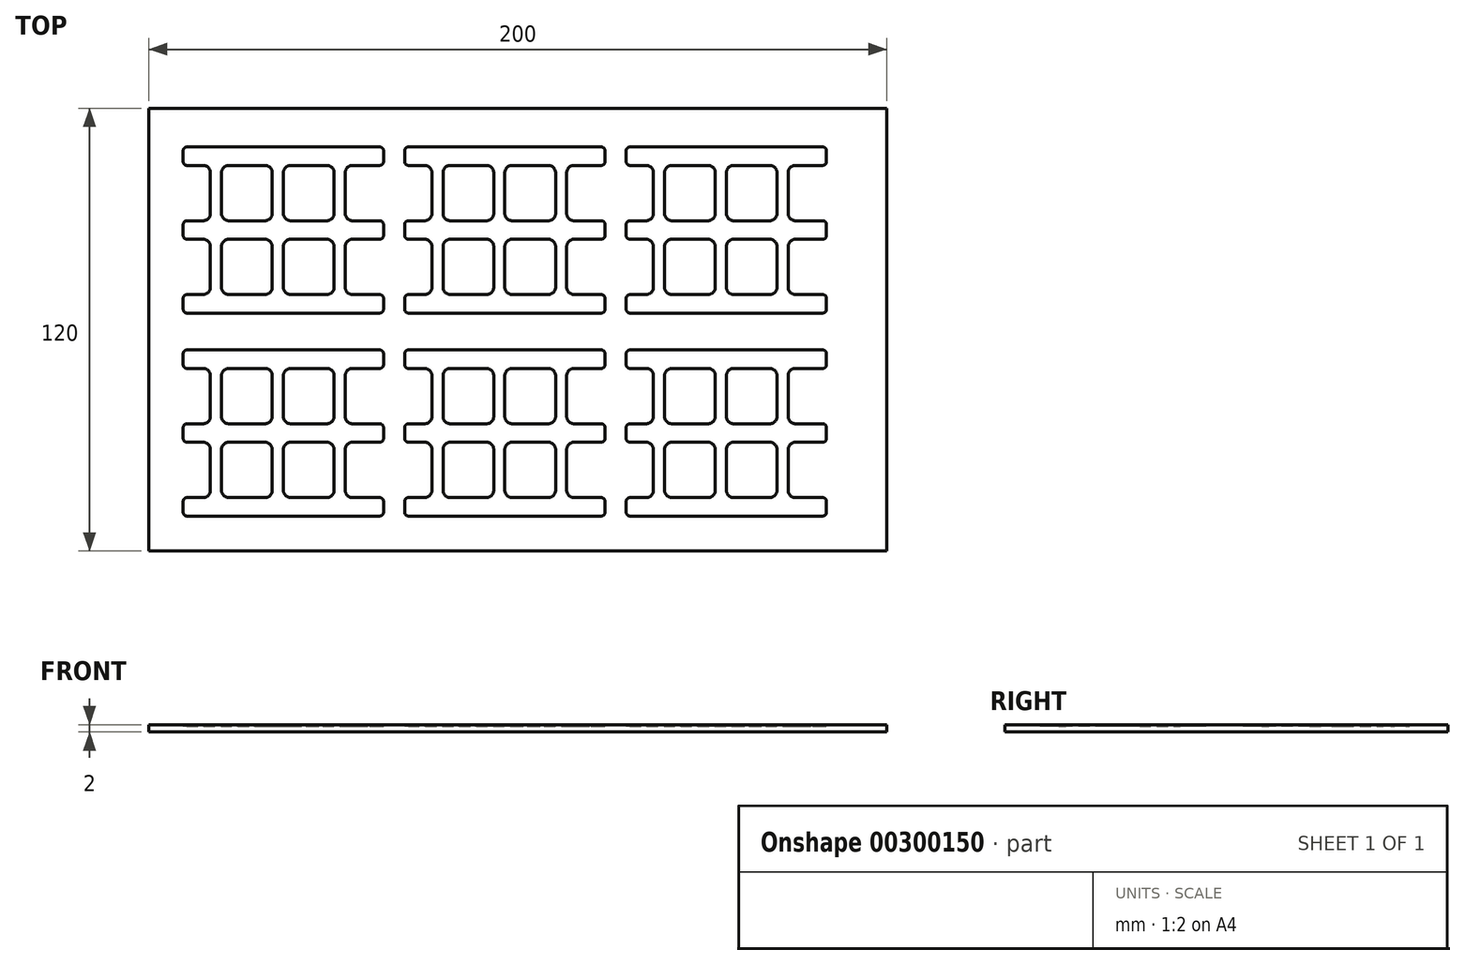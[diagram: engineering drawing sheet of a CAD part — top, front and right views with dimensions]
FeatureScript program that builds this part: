
annotation { "Feature Type Name" : "Feature", "Feature Type Description" : "" }
export const myFeature = defineFeature(function(context is Context, id is Id, definition is map)
    precondition{}
    {
        {
            var Q0;
            Q0=qCreatedBy(makeId("Top.planeOp"),FACE);
            var sketch = newSketch(context, id + "F0", { "sketchPlane" : qUnion([Q0])});
            skLineSegment(sketch, "E0.bottom", {"start": v(-3.5, 2.5) * mm, "end": v(-13.25, 2.5) * mm});
            skLineSegment(sketch, "E0.top", {"start": v(-3.5, 17.5) * mm, "end": v(-13.25, 17.5) * mm});
            skLineSegment(sketch, "E0.left", {"start": v(-1.5, 4.5) * mm, "end": v(-1.5, 15.5) * mm});
            skLineSegment(sketch, "E0.right", {"start": v(-15.25, 4.5) * mm, "end": v(-15.25, 15.5) * mm});
            skPoint(sketch, "E1.visualSharp", {"position": v(-15.25, 17.5) * mm});
            skArc(sketch, "E1.filletArc", {"start": v(-13.25, 17.5) * mm, "mid": v(-14.66, 16.91) * mm, "end": v(-15.25, 15.5) * mm});
            skPoint(sketch, "E2.visualSharp", {"position": v(-1.5, 17.5) * mm});
            skArc(sketch, "E2.filletArc", {"start": v(-1.5, 15.5) * mm, "mid": v(-2.09, 16.91) * mm, "end": v(-3.5, 17.5) * mm});
            skPoint(sketch, "E3.visualSharp", {"position": v(-1.5, 2.5) * mm});
            skArc(sketch, "E3.filletArc", {"start": v(-3.5, 2.5) * mm, "mid": v(-2.09, 3.09) * mm, "end": v(-1.5, 4.5) * mm});
            skPoint(sketch, "E4.visualSharp", {"position": v(-15.25, 2.5) * mm});
            skArc(sketch, "E4.filletArc", {"start": v(-15.25, 4.5) * mm, "mid": v(-14.66, 3.09) * mm, "end": v(-13.25, 2.5) * mm});
            skArc(sketch, "E5.MirrorCS", {"start": v(15.25, 4.5) * mm, "mid": v(14.66, 3.09) * mm, "end": v(13.25, 2.5) * mm});
            skArc(sketch, "E6.MirrorCS", {"start": v(13.25, 17.5) * mm, "mid": v(14.66, 16.91) * mm, "end": v(15.25, 15.5) * mm});
            skArc(sketch, "E7.MirrorCS", {"start": v(3.5, 2.5) * mm, "mid": v(2.09, 3.09) * mm, "end": v(1.5, 4.5) * mm});
            skArc(sketch, "E8.MirrorCS", {"start": v(1.5, 15.5) * mm, "mid": v(2.09, 16.91) * mm, "end": v(3.5, 17.5) * mm});
            skLineSegment(sketch, "E9.MirrorCS", {"start": v(3.5, 17.5) * mm, "end": v(13.25, 17.5) * mm});
            skLineSegment(sketch, "E10.MirrorCS", {"start": v(1.5, 4.5) * mm, "end": v(1.5, 15.5) * mm});
            skPoint(sketch, "E11.MirrorP", {"position": v(1.5, 17.5) * mm});
            skPoint(sketch, "E12.MirrorP", {"position": v(15.25, 2.5) * mm});
            skPoint(sketch, "E13.MirrorP", {"position": v(15.25, 17.5) * mm});
            skPoint(sketch, "E14.MirrorP", {"position": v(1.5, 2.5) * mm});
            skLineSegment(sketch, "E15.MirrorCS", {"start": v(3.5, 2.5) * mm, "end": v(13.25, 2.5) * mm});
            skLineSegment(sketch, "E16.MirrorCS", {"start": v(15.25, 4.5) * mm, "end": v(15.25, 15.5) * mm});
            skArc(sketch, "E17.MirrorCS", {"start": v(-1.5, -15.5) * mm, "mid": v(-2.09, -16.91) * mm, "end": v(-3.5, -17.5) * mm});
            skArc(sketch, "E18.MirrorCS", {"start": v(-3.5, -2.5) * mm, "mid": v(-2.09, -3.09) * mm, "end": v(-1.5, -4.5) * mm});
            skArc(sketch, "E19.MirrorCS", {"start": v(-13.25, -17.5) * mm, "mid": v(-14.66, -16.91) * mm, "end": v(-15.25, -15.5) * mm});
            skArc(sketch, "E20.MirrorCS", {"start": v(15.25, -4.5) * mm, "mid": v(14.66, -3.09) * mm, "end": v(13.25, -2.5) * mm});
            skArc(sketch, "E21.MirrorCS", {"start": v(-15.25, -4.5) * mm, "mid": v(-14.66, -3.09) * mm, "end": v(-13.25, -2.5) * mm});
            skArc(sketch, "E22.MirrorCS", {"start": v(13.25, -17.5) * mm, "mid": v(14.66, -16.91) * mm, "end": v(15.25, -15.5) * mm});
            skArc(sketch, "E23.MirrorCS", {"start": v(3.5, -2.5) * mm, "mid": v(2.09, -3.09) * mm, "end": v(1.5, -4.5) * mm});
            skArc(sketch, "E24.MirrorCS", {"start": v(1.5, -15.5) * mm, "mid": v(2.09, -16.91) * mm, "end": v(3.5, -17.5) * mm});
            skPoint(sketch, "E25.MirrorP", {"position": v(-15.25, -2.5) * mm});
            skLineSegment(sketch, "E26.MirrorCS", {"start": v(-1.5, -4.5) * mm, "end": v(-1.5, -15.5) * mm});
            skLineSegment(sketch, "E27.MirrorCS", {"start": v(15.25, -4.5) * mm, "end": v(15.25, -15.5) * mm});
            skPoint(sketch, "E28.MirrorP", {"position": v(-15.25, -17.5) * mm});
            skLineSegment(sketch, "E29.MirrorCS", {"start": v(3.5, -17.5) * mm, "end": v(13.25, -17.5) * mm});
            skLineSegment(sketch, "E30.MirrorCS", {"start": v(-15.25, -4.5) * mm, "end": v(-15.25, -15.5) * mm});
            skLineSegment(sketch, "E31.MirrorCS", {"start": v(-3.5, -17.5) * mm, "end": v(-13.25, -17.5) * mm});
            skPoint(sketch, "E32.MirrorP", {"position": v(-1.5, -17.5) * mm});
            skLineSegment(sketch, "E33.MirrorCS", {"start": v(1.5, -4.5) * mm, "end": v(1.5, -15.5) * mm});
            skLineSegment(sketch, "E34.MirrorCS", {"start": v(-3.5, -2.5) * mm, "end": v(-13.25, -2.5) * mm});
            skPoint(sketch, "E35.MirrorP", {"position": v(1.5, -17.5) * mm});
            skPoint(sketch, "E36.MirrorP", {"position": v(-1.5, -2.5) * mm});
            skPoint(sketch, "E37.MirrorP", {"position": v(15.25, -2.5) * mm});
            skPoint(sketch, "E38.MirrorP", {"position": v(15.25, -17.5) * mm});
            skPoint(sketch, "E39.MirrorP", {"position": v(1.5, -2.5) * mm});
            skLineSegment(sketch, "E40.MirrorCS", {"start": v(3.5, -2.5) * mm, "end": v(13.25, -2.5) * mm});
            skLineSegment(sketch, "E41", {"start": v(16.75, 36.36) * mm, "end": v(16.75, -33.16) * mm, "construction": true});
            skArc(sketch, "E42.MirrorCS", {"start": v(18.25, 4.5) * mm, "mid": v(18.84, 3.09) * mm, "end": v(20.25, 2.5) * mm});
            skArc(sketch, "E43.MirrorCS", {"start": v(20.25, -17.5) * mm, "mid": v(18.84, -16.91) * mm, "end": v(18.25, -15.5) * mm});
            skArc(sketch, "E44.MirrorCS", {"start": v(20.25, 17.5) * mm, "mid": v(18.84, 16.91) * mm, "end": v(18.25, 15.5) * mm});
            skArc(sketch, "E45.MirrorCS", {"start": v(18.25, -4.5) * mm, "mid": v(18.84, -3.09) * mm, "end": v(20.25, -2.5) * mm});
            skLineSegment(sketch, "E46.MirrorCS", {"start": v(25.63, -2.5) * mm, "end": v(20.25, -2.5) * mm});
            skLineSegment(sketch, "E47.MirrorCS", {"start": v(18.25, -4.5) * mm, "end": v(18.25, -15.5) * mm});
            skPoint(sketch, "E48.MirrorP", {"position": v(18.25, 2.5) * mm});
            skPoint(sketch, "E49.MirrorP", {"position": v(18.25, -2.5) * mm});
            skLineSegment(sketch, "E50.MirrorCS", {"start": v(25.63, 17.5) * mm, "end": v(20.25, 17.5) * mm});
            skPoint(sketch, "E51.MirrorP", {"position": v(18.25, -17.5) * mm});
            skLineSegment(sketch, "E52.MirrorCS", {"start": v(25.63, -17.5) * mm, "end": v(20.25, -17.5) * mm});
            skLineSegment(sketch, "E53.MirrorCS", {"start": v(18.25, 4.5) * mm, "end": v(18.25, 15.5) * mm});
            skPoint(sketch, "E54.MirrorP", {"position": v(18.25, 17.5) * mm});
            skLineSegment(sketch, "E55.MirrorCS", {"start": v(25.63, 2.5) * mm, "end": v(20.25, 2.5) * mm});
            skLineSegment(sketch, "E56.bottom", {"start": v(25.63, 22.5) * mm, "end": v(-24.62, 22.5) * mm});
            skLineSegment(sketch, "E56.top", {"start": v(25.63, -22.5) * mm, "end": v(-24.62, -22.5) * mm});
            skLineSegment(sketch, "E56.left", {"start": v(25.63, 22.5) * mm, "end": v(25.63, 17.5) * mm});
            skPoint(sketch, "E56.middle", {"position": v(0, 0) * mm});
            skArc(sketch, "E57.MirrorCS", {"start": v(-18.25, 4.5) * mm, "mid": v(-18.84, 3.09) * mm, "end": v(-20.25, 2.5) * mm});
            skArc(sketch, "E58.MirrorCS", {"start": v(-18.25, -4.5) * mm, "mid": v(-18.84, -3.09) * mm, "end": v(-20.25, -2.5) * mm});
            skArc(sketch, "E59.MirrorCS", {"start": v(-20.25, 17.5) * mm, "mid": v(-18.84, 16.91) * mm, "end": v(-18.25, 15.5) * mm});
            skArc(sketch, "E60.MirrorCS", {"start": v(-20.25, -17.5) * mm, "mid": v(-18.84, -16.91) * mm, "end": v(-18.25, -15.5) * mm});
            skPoint(sketch, "E61.MirrorP", {"position": v(-18.25, -2.5) * mm});
            skLineSegment(sketch, "E62.MirrorCS", {"start": v(-18.25, -4.5) * mm, "end": v(-18.25, -15.5) * mm});
            skLineSegment(sketch, "E63.MirrorCS", {"start": v(-24.62, -2.5) * mm, "end": v(-20.25, -2.5) * mm});
            skPoint(sketch, "E64.MirrorP", {"position": v(-18.25, 2.5) * mm});
            skPoint(sketch, "E65.MirrorP", {"position": v(-18.25, 17.5) * mm});
            skLineSegment(sketch, "E66.MirrorCS", {"start": v(-25.63, 21.5) * mm, "end": v(-25.63, 18.5) * mm});
            skPoint(sketch, "E67.MirrorP", {"position": v(-18.25, -17.5) * mm});
            skLineSegment(sketch, "E68.MirrorCS", {"start": v(-24.62, 2.5) * mm, "end": v(-20.25, 2.5) * mm});
            skLineSegment(sketch, "E69.MirrorCS", {"start": v(-24.62, -17.5) * mm, "end": v(-20.25, -17.5) * mm});
            skLineSegment(sketch, "E70.MirrorCS", {"start": v(-24.62, 17.5) * mm, "end": v(-20.25, 17.5) * mm});
            skLineSegment(sketch, "E71.MirrorCS", {"start": v(-18.25, 4.5) * mm, "end": v(-18.25, 15.5) * mm});
            skLineSegment(sketch, "E72.trimOffspring", {"start": v(25.63, 2.5) * mm, "end": v(25.63, -2.5) * mm});
            skLineSegment(sketch, "E73.trimOffspring", {"start": v(25.63, -17.5) * mm, "end": v(25.63, -22.5) * mm});
            skLineSegment(sketch, "E74.trimOffspring", {"start": v(-25.63, 1.5) * mm, "end": v(-25.63, -1.5) * mm});
            skLineSegment(sketch, "E75.trimOffspring", {"start": v(-25.63, -18.5) * mm, "end": v(-25.63, -21.5) * mm});
            skLineSegment(sketch, "E76.bottom", {"start": v(25.63, 22.5) * mm, "end": v(27.62, 22.5) * mm});
            skLineSegment(sketch, "E76.top", {"start": v(25.63, 17.5) * mm, "end": v(27.62, 17.5) * mm});
            skLineSegment(sketch, "E76.right", {"start": v(28.62, 21.5) * mm, "end": v(28.62, 18.5) * mm});
            skLineSegment(sketch, "E77.bottom", {"start": v(25.63, 2.5) * mm, "end": v(27.62, 2.5) * mm});
            skLineSegment(sketch, "E77.top", {"start": v(25.63, -2.5) * mm, "end": v(27.62, -2.5) * mm});
            skLineSegment(sketch, "E77.right", {"start": v(28.62, 1.5) * mm, "end": v(28.62, -1.5) * mm});
            skLineSegment(sketch, "E78.bottom", {"start": v(25.63, -17.5) * mm, "end": v(27.63, -17.5) * mm});
            skLineSegment(sketch, "E78.top", {"start": v(25.63, -22.5) * mm, "end": v(27.63, -22.5) * mm});
            skLineSegment(sketch, "E78.right", {"start": v(28.63, -18.5) * mm, "end": v(28.63, -21.5) * mm});
            skArc(sketch, "E79.filletArc", {"start": v(-24.62, 22.5) * mm, "mid": v(-25.33, 22.2) * mm, "end": v(-25.63, 21.5) * mm});
            skPoint(sketch, "E80.visualSharp", {"position": v(-25.63, 17.5) * mm});
            skArc(sketch, "E80.filletArc", {"start": v(-25.63, 18.5) * mm, "mid": v(-25.33, 17.8) * mm, "end": v(-24.62, 17.5) * mm});
            skPoint(sketch, "E81.visualSharp", {"position": v(-25.63, 2.5) * mm});
            skArc(sketch, "E81.filletArc", {"start": v(-24.62, 2.5) * mm, "mid": v(-25.33, 2.2) * mm, "end": v(-25.63, 1.5) * mm});
            skPoint(sketch, "E82.visualSharp", {"position": v(-25.63, -2.5) * mm});
            skArc(sketch, "E82.filletArc", {"start": v(-25.63, -1.5) * mm, "mid": v(-25.33, -2.2) * mm, "end": v(-24.62, -2.5) * mm});
            skPoint(sketch, "E83.visualSharp", {"position": v(-25.63, -22.5) * mm});
            skArc(sketch, "E83.filletArc", {"start": v(-25.63, -21.5) * mm, "mid": v(-25.33, -22.2) * mm, "end": v(-24.62, -22.5) * mm});
            skPoint(sketch, "E84.visualSharp", {"position": v(-25.63, -17.5) * mm});
            skArc(sketch, "E84.filletArc", {"start": v(-24.62, -17.5) * mm, "mid": v(-25.33, -17.8) * mm, "end": v(-25.63, -18.5) * mm});
            skPoint(sketch, "E85.visualSharp", {"position": v(28.62, -17.5) * mm});
            skArc(sketch, "E85.filletArc", {"start": v(28.63, -18.5) * mm, "mid": v(28.33, -17.8) * mm, "end": v(27.63, -17.5) * mm});
            skPoint(sketch, "E86.visualSharp", {"position": v(28.63, -22.5) * mm});
            skArc(sketch, "E86.filletArc", {"start": v(27.63, -22.5) * mm, "mid": v(28.33, -22.2) * mm, "end": v(28.62, -21.5) * mm});
            skPoint(sketch, "E87.visualSharp", {"position": v(28.62, 2.5) * mm});
            skArc(sketch, "E87.filletArc", {"start": v(28.62, 1.5) * mm, "mid": v(28.33, 2.2) * mm, "end": v(27.62, 2.5) * mm});
            skPoint(sketch, "E88.visualSharp", {"position": v(28.62, -2.5) * mm});
            skArc(sketch, "E88.filletArc", {"start": v(27.62, -2.5) * mm, "mid": v(28.33, -2.2) * mm, "end": v(28.63, -1.5) * mm});
            skPoint(sketch, "E89.visualSharp", {"position": v(28.62, 17.5) * mm});
            skArc(sketch, "E89.filletArc", {"start": v(27.62, 17.5) * mm, "mid": v(28.33, 17.8) * mm, "end": v(28.62, 18.5) * mm});
            skArc(sketch, "E90.filletArc", {"start": v(28.62, 21.5) * mm, "mid": v(28.33, 22.2) * mm, "end": v(27.62, 22.5) * mm});
            skPoint(sketch, "E91.0.1.0", {"position": v(-15.25, 72.5) * mm});
            skPoint(sketch, "E91.0.1.1", {"position": v(1.5, 57.5) * mm});
            skPoint(sketch, "E91.0.1.2", {"position": v(28.62, 57.5) * mm});
            skLineSegment(sketch, "E91.0.1.3", {"start": v(25.63, 77.5) * mm, "end": v(-24.62, 77.5) * mm});
            skLineSegment(sketch, "E91.0.1.4", {"start": v(-15.25, 50.5) * mm, "end": v(-15.25, 39.5) * mm});
            skLineSegment(sketch, "E91.0.1.5", {"start": v(1.5, 50.5) * mm, "end": v(1.5, 39.5) * mm});
            skPoint(sketch, "E91.0.1.6", {"position": v(-1.5, 57.5) * mm});
            skPoint(sketch, "E91.0.1.7", {"position": v(28.62, 72.5) * mm});
            skPoint(sketch, "E91.0.1.8", {"position": v(-25.63, 57.5) * mm});
            skPoint(sketch, "E91.0.1.9", {"position": v(18.25, 57.5) * mm});
            skLineSegment(sketch, "E91.0.1.10", {"start": v(25.63, 32.5) * mm, "end": v(-24.62, 32.5) * mm});
            skLineSegment(sketch, "E91.0.1.11", {"start": v(-3.5, 37.5) * mm, "end": v(-13.25, 37.5) * mm});
            skLineSegment(sketch, "E91.0.1.12", {"start": v(-3.5, 52.5) * mm, "end": v(-13.25, 52.5) * mm});
            skPoint(sketch, "E91.0.1.13", {"position": v(-1.5, 72.5) * mm});
            skPoint(sketch, "E91.0.1.14", {"position": v(28.62, 52.5) * mm});
            skPoint(sketch, "E91.0.1.15", {"position": v(-25.63, 72.5) * mm});
            skPoint(sketch, "E91.0.1.16", {"position": v(18.25, 52.5) * mm});
            skLineSegment(sketch, "E91.0.1.17", {"start": v(3.5, 52.5) * mm, "end": v(13.25, 52.5) * mm});
            skLineSegment(sketch, "E91.0.1.18", {"start": v(1.5, 59.5) * mm, "end": v(1.5, 70.5) * mm});
            skLineSegment(sketch, "E91.0.1.19", {"start": v(3.5, 57.5) * mm, "end": v(13.25, 57.5) * mm});
            skLineSegment(sketch, "E91.0.1.20", {"start": v(15.25, 59.5) * mm, "end": v(15.25, 70.5) * mm});
            skLineSegment(sketch, "E91.0.1.21", {"start": v(-1.5, 59.5) * mm, "end": v(-1.5, 70.5) * mm});
            skLineSegment(sketch, "E91.0.1.22", {"start": v(-15.25, 59.5) * mm, "end": v(-15.25, 70.5) * mm});
            skLineSegment(sketch, "E91.0.1.23", {"start": v(3.5, 72.5) * mm, "end": v(13.25, 72.5) * mm});
            skPoint(sketch, "E91.0.1.24", {"position": v(-15.25, 57.5) * mm});
            skPoint(sketch, "E91.0.1.25", {"position": v(-25.63, 52.5) * mm});
            skPoint(sketch, "E91.0.1.26", {"position": v(18.25, 37.5) * mm});
            skLineSegment(sketch, "E91.0.1.27", {"start": v(16.75, 91.36) * mm, "end": v(16.75, 21.84) * mm, "construction": true});
            skPoint(sketch, "E91.0.1.28", {"position": v(18.25, 72.5) * mm});
            skPoint(sketch, "E91.0.1.29", {"position": v(-15.25, 52.5) * mm});
            skPoint(sketch, "E91.0.1.30", {"position": v(-25.63, 32.5) * mm});
            skPoint(sketch, "E91.0.1.31", {"position": v(0, 55) * mm});
            skLineSegment(sketch, "E91.0.1.32", {"start": v(-18.25, 50.5) * mm, "end": v(-18.25, 39.5) * mm});
            skPoint(sketch, "E91.0.1.33", {"position": v(-18.25, 37.5) * mm});
            skPoint(sketch, "E91.0.1.34", {"position": v(1.5, 52.5) * mm});
            skPoint(sketch, "E91.0.1.35", {"position": v(-15.25, 37.5) * mm});
            skPoint(sketch, "E91.0.1.36", {"position": v(-1.5, 37.5) * mm});
            skPoint(sketch, "E91.0.1.37", {"position": v(-25.63, 37.5) * mm});
            skPoint(sketch, "E91.0.1.38", {"position": v(1.5, 37.5) * mm});
            skPoint(sketch, "E91.0.1.39", {"position": v(-1.5, 52.5) * mm});
            skPoint(sketch, "E91.0.1.40", {"position": v(1.5, 72.5) * mm});
            skPoint(sketch, "E91.0.1.41", {"position": v(28.62, 37.5) * mm});
            skLineSegment(sketch, "E91.0.1.42", {"start": v(18.25, 50.5) * mm, "end": v(18.25, 39.5) * mm});
            skPoint(sketch, "E91.0.1.43", {"position": v(15.25, 52.5) * mm});
            skPoint(sketch, "E91.0.1.44", {"position": v(15.25, 57.5) * mm});
            skPoint(sketch, "E91.0.1.45", {"position": v(28.63, 32.5) * mm});
            skPoint(sketch, "E91.0.1.46", {"position": v(15.25, 37.5) * mm});
            skPoint(sketch, "E91.0.1.47", {"position": v(15.25, 72.5) * mm});
            skLineSegment(sketch, "E91.0.1.48", {"start": v(-18.25, 59.5) * mm, "end": v(-18.25, 70.5) * mm});
            skLineSegment(sketch, "E91.0.1.49", {"start": v(-1.5, 50.5) * mm, "end": v(-1.5, 39.5) * mm});
            skLineSegment(sketch, "E91.0.1.50", {"start": v(18.25, 59.5) * mm, "end": v(18.25, 70.5) * mm});
            skLineSegment(sketch, "E91.0.1.51", {"start": v(15.25, 50.5) * mm, "end": v(15.25, 39.5) * mm});
            skLineSegment(sketch, "E91.0.1.52", {"start": v(3.5, 37.5) * mm, "end": v(13.25, 37.5) * mm});
            skPoint(sketch, "E91.0.1.53", {"position": v(-18.25, 72.5) * mm});
            skLineSegment(sketch, "E91.0.1.54", {"start": v(-3.5, 57.5) * mm, "end": v(-13.25, 57.5) * mm});
            skLineSegment(sketch, "E91.0.1.55", {"start": v(-3.5, 72.5) * mm, "end": v(-13.25, 72.5) * mm});
            skPoint(sketch, "E91.0.1.56", {"position": v(-18.25, 52.5) * mm});
            skPoint(sketch, "E91.0.1.57", {"position": v(-18.25, 57.5) * mm});
            skArc(sketch, "E91.0.1.58", {"start": v(-1.5, 70.5) * mm, "mid": v(-2.09, 71.91) * mm, "end": v(-3.5, 72.5) * mm});
            skArc(sketch, "E91.0.1.59", {"start": v(1.5, 70.5) * mm, "mid": v(2.09, 71.91) * mm, "end": v(3.5, 72.5) * mm});
            skArc(sketch, "E91.0.1.60", {"start": v(-1.5, 39.5) * mm, "mid": v(-2.09, 38.09) * mm, "end": v(-3.5, 37.5) * mm});
            skArc(sketch, "E91.0.1.61", {"start": v(-3.5, 52.5) * mm, "mid": v(-2.09, 51.91) * mm, "end": v(-1.5, 50.5) * mm});
            skArc(sketch, "E91.0.1.62", {"start": v(-13.25, 37.5) * mm, "mid": v(-14.66, 38.09) * mm, "end": v(-15.25, 39.5) * mm});
            skArc(sketch, "E91.0.1.63", {"start": v(-24.62, 57.5) * mm, "mid": v(-25.33, 57.2) * mm, "end": v(-25.63, 56.5) * mm});
            skArc(sketch, "E91.0.1.64", {"start": v(-13.25, 72.5) * mm, "mid": v(-14.66, 71.91) * mm, "end": v(-15.25, 70.5) * mm});
            skArc(sketch, "E91.0.1.65", {"start": v(-3.5, 57.5) * mm, "mid": v(-2.09, 58.09) * mm, "end": v(-1.5, 59.5) * mm});
            skArc(sketch, "E91.0.1.66", {"start": v(13.25, 72.5) * mm, "mid": v(14.66, 71.91) * mm, "end": v(15.25, 70.5) * mm});
            skArc(sketch, "E91.0.1.67", {"start": v(3.5, 57.5) * mm, "mid": v(2.09, 58.09) * mm, "end": v(1.5, 59.5) * mm});
            skArc(sketch, "E91.0.1.68", {"start": v(-20.25, 72.5) * mm, "mid": v(-18.84, 71.91) * mm, "end": v(-18.25, 70.5) * mm});
            skArc(sketch, "E91.0.1.69", {"start": v(-20.25, 37.5) * mm, "mid": v(-18.84, 38.09) * mm, "end": v(-18.25, 39.5) * mm});
            skArc(sketch, "E91.0.1.70", {"start": v(20.25, 37.5) * mm, "mid": v(18.84, 38.09) * mm, "end": v(18.25, 39.5) * mm});
            skArc(sketch, "E91.0.1.71", {"start": v(15.25, 50.5) * mm, "mid": v(14.66, 51.91) * mm, "end": v(13.25, 52.5) * mm});
            skArc(sketch, "E91.0.1.72", {"start": v(20.25, 72.5) * mm, "mid": v(18.84, 71.91) * mm, "end": v(18.25, 70.5) * mm});
            skArc(sketch, "E91.0.1.73", {"start": v(-15.25, 50.5) * mm, "mid": v(-14.66, 51.91) * mm, "end": v(-13.25, 52.5) * mm});
            skLineSegment(sketch, "E91.0.1.74", {"start": v(-25.63, 76.5) * mm, "end": v(-25.63, 73.5) * mm});
            skArc(sketch, "E91.0.1.75", {"start": v(18.25, 50.5) * mm, "mid": v(18.84, 51.91) * mm, "end": v(20.25, 52.5) * mm});
            skArc(sketch, "E91.0.1.76", {"start": v(13.25, 37.5) * mm, "mid": v(14.66, 38.09) * mm, "end": v(15.25, 39.5) * mm});
            skLineSegment(sketch, "E91.0.1.77", {"start": v(-24.62, 57.5) * mm, "end": v(-20.25, 57.5) * mm});
            skLineSegment(sketch, "E91.0.1.78", {"start": v(25.63, 52.5) * mm, "end": v(20.25, 52.5) * mm});
            skArc(sketch, "E91.0.1.79", {"start": v(3.5, 52.5) * mm, "mid": v(2.09, 51.91) * mm, "end": v(1.5, 50.5) * mm});
            skLineSegment(sketch, "E91.0.1.80", {"start": v(-24.62, 72.5) * mm, "end": v(-20.25, 72.5) * mm});
            skLineSegment(sketch, "E91.0.1.81", {"start": v(25.63, 72.5) * mm, "end": v(20.25, 72.5) * mm});
            skArc(sketch, "E91.0.1.82", {"start": v(1.5, 39.5) * mm, "mid": v(2.09, 38.09) * mm, "end": v(3.5, 37.5) * mm});
            skLineSegment(sketch, "E91.0.1.83", {"start": v(25.63, 37.5) * mm, "end": v(20.25, 37.5) * mm});
            skArc(sketch, "E91.0.1.84", {"start": v(-24.62, 77.5) * mm, "mid": v(-25.33, 77.2) * mm, "end": v(-25.63, 76.5) * mm});
            skArc(sketch, "E91.0.1.85", {"start": v(-25.63, 73.5) * mm, "mid": v(-25.33, 72.8) * mm, "end": v(-24.62, 72.5) * mm});
            skLineSegment(sketch, "E91.0.1.86", {"start": v(-25.63, 56.5) * mm, "end": v(-25.63, 53.5) * mm});
            skArc(sketch, "E91.0.1.87", {"start": v(-25.63, 33.5) * mm, "mid": v(-25.33, 32.8) * mm, "end": v(-24.62, 32.5) * mm});
            skLineSegment(sketch, "E91.0.1.88", {"start": v(-25.63, 36.5) * mm, "end": v(-25.63, 33.5) * mm});
            skArc(sketch, "E91.0.1.89", {"start": v(-25.63, 53.5) * mm, "mid": v(-25.33, 52.8) * mm, "end": v(-24.62, 52.5) * mm});
            skArc(sketch, "E91.0.1.90", {"start": v(-24.62, 37.5) * mm, "mid": v(-25.33, 37.2) * mm, "end": v(-25.63, 36.5) * mm});
            skArc(sketch, "E91.0.1.91", {"start": v(-18.25, 59.5) * mm, "mid": v(-18.84, 58.09) * mm, "end": v(-20.25, 57.5) * mm});
            skArc(sketch, "E91.0.1.92", {"start": v(-18.25, 50.5) * mm, "mid": v(-18.84, 51.91) * mm, "end": v(-20.25, 52.5) * mm});
            skArc(sketch, "E91.0.1.93", {"start": v(-15.25, 59.5) * mm, "mid": v(-14.66, 58.09) * mm, "end": v(-13.25, 57.5) * mm});
            skArc(sketch, "E91.0.1.94", {"start": v(15.25, 59.5) * mm, "mid": v(14.66, 58.09) * mm, "end": v(13.25, 57.5) * mm});
            skLineSegment(sketch, "E91.0.1.95", {"start": v(-24.62, 52.5) * mm, "end": v(-20.25, 52.5) * mm});
            skLineSegment(sketch, "E91.0.1.96", {"start": v(-24.62, 37.5) * mm, "end": v(-20.25, 37.5) * mm});
            skLineSegment(sketch, "E91.0.1.97", {"start": v(25.63, 57.5) * mm, "end": v(20.25, 57.5) * mm});
            skLineSegment(sketch, "E91.0.1.98", {"start": v(25.63, 37.5) * mm, "end": v(25.63, 32.5) * mm});
            skLineSegment(sketch, "E91.0.1.99", {"start": v(25.63, 77.5) * mm, "end": v(27.62, 77.5) * mm});
            skLineSegment(sketch, "E91.0.1.100", {"start": v(25.63, 72.5) * mm, "end": v(27.62, 72.5) * mm});
            skArc(sketch, "E91.0.1.101", {"start": v(28.63, 36.5) * mm, "mid": v(28.33, 37.2) * mm, "end": v(27.63, 37.5) * mm});
            skLineSegment(sketch, "E91.0.1.102", {"start": v(25.63, 77.5) * mm, "end": v(25.63, 72.5) * mm});
            skArc(sketch, "E91.0.1.103", {"start": v(27.63, 32.5) * mm, "mid": v(28.33, 32.8) * mm, "end": v(28.62, 33.5) * mm});
            skLineSegment(sketch, "E91.0.1.104", {"start": v(28.62, 76.5) * mm, "end": v(28.62, 73.5) * mm});
            skArc(sketch, "E91.0.1.105", {"start": v(28.62, 56.5) * mm, "mid": v(28.33, 57.2) * mm, "end": v(27.62, 57.5) * mm});
            skLineSegment(sketch, "E91.0.1.106", {"start": v(25.63, 57.5) * mm, "end": v(27.62, 57.5) * mm});
            skArc(sketch, "E91.0.1.107", {"start": v(18.25, 59.5) * mm, "mid": v(18.84, 58.09) * mm, "end": v(20.25, 57.5) * mm});
            skArc(sketch, "E91.0.1.108", {"start": v(27.62, 72.5) * mm, "mid": v(28.33, 72.8) * mm, "end": v(28.62, 73.5) * mm});
            skArc(sketch, "E91.0.1.109", {"start": v(28.62, 76.5) * mm, "mid": v(28.33, 77.2) * mm, "end": v(27.62, 77.5) * mm});
            skLineSegment(sketch, "E91.0.1.110", {"start": v(25.63, 37.5) * mm, "end": v(27.63, 37.5) * mm});
            skLineSegment(sketch, "E91.0.1.111", {"start": v(25.63, 32.5) * mm, "end": v(27.63, 32.5) * mm});
            skLineSegment(sketch, "E91.0.1.112", {"start": v(28.63, 36.5) * mm, "end": v(28.63, 33.5) * mm});
            skLineSegment(sketch, "E91.0.1.113", {"start": v(25.63, 77.5) * mm, "end": v(25.63, 72.5) * mm});
            skArc(sketch, "E91.0.1.114", {"start": v(27.62, 52.5) * mm, "mid": v(28.33, 52.8) * mm, "end": v(28.63, 53.5) * mm});
            skLineSegment(sketch, "E91.0.1.115", {"start": v(25.63, 52.5) * mm, "end": v(27.62, 52.5) * mm});
            skLineSegment(sketch, "E91.0.1.116", {"start": v(28.62, 56.5) * mm, "end": v(28.62, 53.5) * mm});
            skLineSegment(sketch, "E91.0.1.117", {"start": v(25.63, 37.5) * mm, "end": v(25.63, 32.5) * mm});
            skLineSegment(sketch, "E91.0.1.118", {"start": v(25.63, 57.5) * mm, "end": v(25.63, 52.5) * mm});
            skLineSegment(sketch, "E91.0.1.119", {"start": v(25.63, 57.5) * mm, "end": v(25.63, 52.5) * mm});
            skPoint(sketch, "E91.1.0.0", {"position": v(44.75, 17.5) * mm});
            skPoint(sketch, "E91.1.0.1", {"position": v(61.5, 2.5) * mm});
            skPoint(sketch, "E91.1.0.2", {"position": v(88.62, 2.5) * mm});
            skLineSegment(sketch, "E91.1.0.3", {"start": v(85.62, 22.5) * mm, "end": v(35.38, 22.5) * mm});
            skLineSegment(sketch, "E91.1.0.4", {"start": v(44.75, -4.5) * mm, "end": v(44.75, -15.5) * mm});
            skLineSegment(sketch, "E91.1.0.5", {"start": v(61.5, -4.5) * mm, "end": v(61.5, -15.5) * mm});
            skPoint(sketch, "E91.1.0.6", {"position": v(58.5, 2.5) * mm});
            skPoint(sketch, "E91.1.0.7", {"position": v(88.62, 17.5) * mm});
            skPoint(sketch, "E91.1.0.8", {"position": v(34.37, 2.5) * mm});
            skPoint(sketch, "E91.1.0.9", {"position": v(78.25, 2.5) * mm});
            skLineSegment(sketch, "E91.1.0.10", {"start": v(85.62, -22.5) * mm, "end": v(35.37, -22.5) * mm});
            skLineSegment(sketch, "E91.1.0.11", {"start": v(56.5, -17.5) * mm, "end": v(46.75, -17.5) * mm});
            skLineSegment(sketch, "E91.1.0.12", {"start": v(56.5, -2.5) * mm, "end": v(46.75, -2.5) * mm});
            skPoint(sketch, "E91.1.0.13", {"position": v(58.5, 17.5) * mm});
            skPoint(sketch, "E91.1.0.14", {"position": v(88.62, -2.5) * mm});
            skPoint(sketch, "E91.1.0.15", {"position": v(34.37, 17.5) * mm});
            skPoint(sketch, "E91.1.0.16", {"position": v(78.25, -2.5) * mm});
            skLineSegment(sketch, "E91.1.0.17", {"start": v(63.5, -2.5) * mm, "end": v(73.25, -2.5) * mm});
            skLineSegment(sketch, "E91.1.0.18", {"start": v(61.5, 4.5) * mm, "end": v(61.5, 15.5) * mm});
            skLineSegment(sketch, "E91.1.0.19", {"start": v(63.5, 2.5) * mm, "end": v(73.25, 2.5) * mm});
            skLineSegment(sketch, "E91.1.0.20", {"start": v(75.25, 4.5) * mm, "end": v(75.25, 15.5) * mm});
            skLineSegment(sketch, "E91.1.0.21", {"start": v(58.5, 4.5) * mm, "end": v(58.5, 15.5) * mm});
            skLineSegment(sketch, "E91.1.0.22", {"start": v(44.75, 4.5) * mm, "end": v(44.75, 15.5) * mm});
            skLineSegment(sketch, "E91.1.0.23", {"start": v(63.5, 17.5) * mm, "end": v(73.25, 17.5) * mm});
            skPoint(sketch, "E91.1.0.24", {"position": v(44.75, 2.5) * mm});
            skPoint(sketch, "E91.1.0.25", {"position": v(34.37, -2.5) * mm});
            skPoint(sketch, "E91.1.0.26", {"position": v(78.25, -17.5) * mm});
            skLineSegment(sketch, "E91.1.0.27", {"start": v(76.75, 36.36) * mm, "end": v(76.75, -33.16) * mm, "construction": true});
            skPoint(sketch, "E91.1.0.28", {"position": v(78.25, 17.5) * mm});
            skPoint(sketch, "E91.1.0.29", {"position": v(44.75, -2.5) * mm});
            skPoint(sketch, "E91.1.0.30", {"position": v(34.37, -22.5) * mm});
            skPoint(sketch, "E91.1.0.31", {"position": v(60, 0) * mm});
            skLineSegment(sketch, "E91.1.0.32", {"start": v(41.75, -4.5) * mm, "end": v(41.75, -15.5) * mm});
            skPoint(sketch, "E91.1.0.33", {"position": v(41.75, -17.5) * mm});
            skPoint(sketch, "E91.1.0.34", {"position": v(61.5, -2.5) * mm});
            skPoint(sketch, "E91.1.0.35", {"position": v(44.75, -17.5) * mm});
            skPoint(sketch, "E91.1.0.36", {"position": v(58.5, -17.5) * mm});
            skPoint(sketch, "E91.1.0.37", {"position": v(34.37, -17.5) * mm});
            skPoint(sketch, "E91.1.0.38", {"position": v(61.5, -17.5) * mm});
            skPoint(sketch, "E91.1.0.39", {"position": v(58.5, -2.5) * mm});
            skPoint(sketch, "E91.1.0.40", {"position": v(61.5, 17.5) * mm});
            skPoint(sketch, "E91.1.0.41", {"position": v(88.62, -17.5) * mm});
            skLineSegment(sketch, "E91.1.0.42", {"start": v(78.25, -4.5) * mm, "end": v(78.25, -15.5) * mm});
            skPoint(sketch, "E91.1.0.43", {"position": v(75.25, -2.5) * mm});
            skPoint(sketch, "E91.1.0.44", {"position": v(75.25, 2.5) * mm});
            skPoint(sketch, "E91.1.0.45", {"position": v(88.63, -22.5) * mm});
            skPoint(sketch, "E91.1.0.46", {"position": v(75.25, -17.5) * mm});
            skPoint(sketch, "E91.1.0.47", {"position": v(75.25, 17.5) * mm});
            skLineSegment(sketch, "E91.1.0.48", {"start": v(41.75, 4.5) * mm, "end": v(41.75, 15.5) * mm});
            skLineSegment(sketch, "E91.1.0.49", {"start": v(58.5, -4.5) * mm, "end": v(58.5, -15.5) * mm});
            skLineSegment(sketch, "E91.1.0.50", {"start": v(78.25, 4.5) * mm, "end": v(78.25, 15.5) * mm});
            skLineSegment(sketch, "E91.1.0.51", {"start": v(75.25, -4.5) * mm, "end": v(75.25, -15.5) * mm});
            skLineSegment(sketch, "E91.1.0.52", {"start": v(63.5, -17.5) * mm, "end": v(73.25, -17.5) * mm});
            skPoint(sketch, "E91.1.0.53", {"position": v(41.75, 17.5) * mm});
            skLineSegment(sketch, "E91.1.0.54", {"start": v(56.5, 2.5) * mm, "end": v(46.75, 2.5) * mm});
            skLineSegment(sketch, "E91.1.0.55", {"start": v(56.5, 17.5) * mm, "end": v(46.75, 17.5) * mm});
            skPoint(sketch, "E91.1.0.56", {"position": v(41.75, -2.5) * mm});
            skPoint(sketch, "E91.1.0.57", {"position": v(41.75, 2.5) * mm});
            skArc(sketch, "E91.1.0.58", {"start": v(58.5, 15.5) * mm, "mid": v(57.91, 16.91) * mm, "end": v(56.5, 17.5) * mm});
            skArc(sketch, "E91.1.0.59", {"start": v(61.5, 15.5) * mm, "mid": v(62.09, 16.91) * mm, "end": v(63.5, 17.5) * mm});
            skArc(sketch, "E91.1.0.60", {"start": v(58.5, -15.5) * mm, "mid": v(57.91, -16.91) * mm, "end": v(56.5, -17.5) * mm});
            skArc(sketch, "E91.1.0.61", {"start": v(56.5, -2.5) * mm, "mid": v(57.91, -3.09) * mm, "end": v(58.5, -4.5) * mm});
            skArc(sketch, "E91.1.0.62", {"start": v(46.75, -17.5) * mm, "mid": v(45.34, -16.91) * mm, "end": v(44.75, -15.5) * mm});
            skArc(sketch, "E91.1.0.63", {"start": v(35.38, 2.5) * mm, "mid": v(34.67, 2.2) * mm, "end": v(34.37, 1.5) * mm});
            skArc(sketch, "E91.1.0.64", {"start": v(46.75, 17.5) * mm, "mid": v(45.34, 16.91) * mm, "end": v(44.75, 15.5) * mm});
            skArc(sketch, "E91.1.0.65", {"start": v(56.5, 2.5) * mm, "mid": v(57.91, 3.09) * mm, "end": v(58.5, 4.5) * mm});
            skArc(sketch, "E91.1.0.66", {"start": v(73.25, 17.5) * mm, "mid": v(74.66, 16.91) * mm, "end": v(75.25, 15.5) * mm});
            skArc(sketch, "E91.1.0.67", {"start": v(63.5, 2.5) * mm, "mid": v(62.09, 3.09) * mm, "end": v(61.5, 4.5) * mm});
            skArc(sketch, "E91.1.0.68", {"start": v(39.75, 17.5) * mm, "mid": v(41.16, 16.91) * mm, "end": v(41.75, 15.5) * mm});
            skArc(sketch, "E91.1.0.69", {"start": v(39.75, -17.5) * mm, "mid": v(41.16, -16.91) * mm, "end": v(41.75, -15.5) * mm});
            skArc(sketch, "E91.1.0.70", {"start": v(80.25, -17.5) * mm, "mid": v(78.84, -16.91) * mm, "end": v(78.25, -15.5) * mm});
            skArc(sketch, "E91.1.0.71", {"start": v(75.25, -4.5) * mm, "mid": v(74.66, -3.09) * mm, "end": v(73.25, -2.5) * mm});
            skArc(sketch, "E91.1.0.72", {"start": v(80.25, 17.5) * mm, "mid": v(78.84, 16.91) * mm, "end": v(78.25, 15.5) * mm});
            skArc(sketch, "E91.1.0.73", {"start": v(44.75, -4.5) * mm, "mid": v(45.34, -3.09) * mm, "end": v(46.75, -2.5) * mm});
            skLineSegment(sketch, "E91.1.0.74", {"start": v(34.37, 21.5) * mm, "end": v(34.37, 18.5) * mm});
            skArc(sketch, "E91.1.0.75", {"start": v(78.25, -4.5) * mm, "mid": v(78.84, -3.09) * mm, "end": v(80.25, -2.5) * mm});
            skArc(sketch, "E91.1.0.76", {"start": v(73.25, -17.5) * mm, "mid": v(74.66, -16.91) * mm, "end": v(75.25, -15.5) * mm});
            skLineSegment(sketch, "E91.1.0.77", {"start": v(35.38, 2.5) * mm, "end": v(39.75, 2.5) * mm});
            skLineSegment(sketch, "E91.1.0.78", {"start": v(85.62, -2.5) * mm, "end": v(80.25, -2.5) * mm});
            skArc(sketch, "E91.1.0.79", {"start": v(63.5, -2.5) * mm, "mid": v(62.09, -3.09) * mm, "end": v(61.5, -4.5) * mm});
            skLineSegment(sketch, "E91.1.0.80", {"start": v(35.38, 17.5) * mm, "end": v(39.75, 17.5) * mm});
            skLineSegment(sketch, "E91.1.0.81", {"start": v(85.62, 17.5) * mm, "end": v(80.25, 17.5) * mm});
            skArc(sketch, "E91.1.0.82", {"start": v(61.5, -15.5) * mm, "mid": v(62.09, -16.91) * mm, "end": v(63.5, -17.5) * mm});
            skLineSegment(sketch, "E91.1.0.83", {"start": v(85.62, -17.5) * mm, "end": v(80.25, -17.5) * mm});
            skArc(sketch, "E91.1.0.84", {"start": v(35.38, 22.5) * mm, "mid": v(34.67, 22.2) * mm, "end": v(34.37, 21.5) * mm});
            skArc(sketch, "E91.1.0.85", {"start": v(34.37, 18.5) * mm, "mid": v(34.67, 17.8) * mm, "end": v(35.38, 17.5) * mm});
            skLineSegment(sketch, "E91.1.0.86", {"start": v(34.37, 1.5) * mm, "end": v(34.37, -1.5) * mm});
            skArc(sketch, "E91.1.0.87", {"start": v(34.37, -21.5) * mm, "mid": v(34.67, -22.2) * mm, "end": v(35.38, -22.5) * mm});
            skLineSegment(sketch, "E91.1.0.88", {"start": v(34.37, -18.5) * mm, "end": v(34.37, -21.5) * mm});
            skArc(sketch, "E91.1.0.89", {"start": v(34.37, -1.5) * mm, "mid": v(34.67, -2.2) * mm, "end": v(35.38, -2.5) * mm});
            skArc(sketch, "E91.1.0.90", {"start": v(35.38, -17.5) * mm, "mid": v(34.67, -17.8) * mm, "end": v(34.37, -18.5) * mm});
            skArc(sketch, "E91.1.0.91", {"start": v(41.75, 4.5) * mm, "mid": v(41.16, 3.09) * mm, "end": v(39.75, 2.5) * mm});
            skArc(sketch, "E91.1.0.92", {"start": v(41.75, -4.5) * mm, "mid": v(41.16, -3.09) * mm, "end": v(39.75, -2.5) * mm});
            skArc(sketch, "E91.1.0.93", {"start": v(44.75, 4.5) * mm, "mid": v(45.34, 3.09) * mm, "end": v(46.75, 2.5) * mm});
            skArc(sketch, "E91.1.0.94", {"start": v(75.25, 4.5) * mm, "mid": v(74.66, 3.09) * mm, "end": v(73.25, 2.5) * mm});
            skLineSegment(sketch, "E91.1.0.95", {"start": v(35.38, -2.5) * mm, "end": v(39.75, -2.5) * mm});
            skLineSegment(sketch, "E91.1.0.96", {"start": v(35.38, -17.5) * mm, "end": v(39.75, -17.5) * mm});
            skLineSegment(sketch, "E91.1.0.97", {"start": v(85.62, 2.5) * mm, "end": v(80.25, 2.5) * mm});
            skLineSegment(sketch, "E91.1.0.98", {"start": v(85.62, -17.5) * mm, "end": v(85.62, -22.5) * mm});
            skLineSegment(sketch, "E91.1.0.99", {"start": v(85.62, 22.5) * mm, "end": v(87.63, 22.5) * mm});
            skLineSegment(sketch, "E91.1.0.100", {"start": v(85.62, 17.5) * mm, "end": v(87.63, 17.5) * mm});
            skArc(sketch, "E91.1.0.101", {"start": v(88.63, -18.5) * mm, "mid": v(88.33, -17.8) * mm, "end": v(87.63, -17.5) * mm});
            skLineSegment(sketch, "E91.1.0.102", {"start": v(85.62, 22.5) * mm, "end": v(85.62, 17.5) * mm});
            skArc(sketch, "E91.1.0.103", {"start": v(87.63, -22.5) * mm, "mid": v(88.33, -22.2) * mm, "end": v(88.63, -21.5) * mm});
            skLineSegment(sketch, "E91.1.0.104", {"start": v(88.62, 21.5) * mm, "end": v(88.62, 18.5) * mm});
            skArc(sketch, "E91.1.0.105", {"start": v(88.63, 1.5) * mm, "mid": v(88.33, 2.2) * mm, "end": v(87.63, 2.5) * mm});
            skLineSegment(sketch, "E91.1.0.106", {"start": v(85.62, 2.5) * mm, "end": v(87.63, 2.5) * mm});
            skArc(sketch, "E91.1.0.107", {"start": v(78.25, 4.5) * mm, "mid": v(78.84, 3.09) * mm, "end": v(80.25, 2.5) * mm});
            skArc(sketch, "E91.1.0.108", {"start": v(87.63, 17.5) * mm, "mid": v(88.33, 17.8) * mm, "end": v(88.63, 18.5) * mm});
            skArc(sketch, "E91.1.0.109", {"start": v(88.63, 21.5) * mm, "mid": v(88.33, 22.2) * mm, "end": v(87.63, 22.5) * mm});
            skLineSegment(sketch, "E91.1.0.110", {"start": v(85.62, -17.5) * mm, "end": v(87.63, -17.5) * mm});
            skLineSegment(sketch, "E91.1.0.111", {"start": v(85.62, -22.5) * mm, "end": v(87.63, -22.5) * mm});
            skLineSegment(sketch, "E91.1.0.112", {"start": v(88.63, -18.5) * mm, "end": v(88.63, -21.5) * mm});
            skLineSegment(sketch, "E91.1.0.113", {"start": v(85.62, 22.5) * mm, "end": v(85.62, 17.5) * mm});
            skArc(sketch, "E91.1.0.114", {"start": v(87.63, -2.5) * mm, "mid": v(88.33, -2.2) * mm, "end": v(88.63, -1.5) * mm});
            skLineSegment(sketch, "E91.1.0.115", {"start": v(85.62, -2.5) * mm, "end": v(87.63, -2.5) * mm});
            skLineSegment(sketch, "E91.1.0.116", {"start": v(88.62, 1.5) * mm, "end": v(88.62, -1.5) * mm});
            skLineSegment(sketch, "E91.1.0.117", {"start": v(85.62, -17.5) * mm, "end": v(85.62, -22.5) * mm});
            skLineSegment(sketch, "E91.1.0.118", {"start": v(85.62, 2.5) * mm, "end": v(85.62, -2.5) * mm});
            skLineSegment(sketch, "E91.1.0.119", {"start": v(85.62, 2.5) * mm, "end": v(85.62, -2.5) * mm});
            skPoint(sketch, "E91.1.1.0", {"position": v(44.75, 72.5) * mm});
            skPoint(sketch, "E91.1.1.1", {"position": v(61.5, 57.5) * mm});
            skPoint(sketch, "E91.1.1.2", {"position": v(88.62, 57.5) * mm});
            skLineSegment(sketch, "E91.1.1.3", {"start": v(85.62, 77.5) * mm, "end": v(35.38, 77.5) * mm});
            skLineSegment(sketch, "E91.1.1.4", {"start": v(44.75, 50.5) * mm, "end": v(44.75, 39.5) * mm});
            skLineSegment(sketch, "E91.1.1.5", {"start": v(61.5, 50.5) * mm, "end": v(61.5, 39.5) * mm});
            skPoint(sketch, "E91.1.1.6", {"position": v(58.5, 57.5) * mm});
            skPoint(sketch, "E91.1.1.7", {"position": v(88.62, 72.5) * mm});
            skPoint(sketch, "E91.1.1.8", {"position": v(34.37, 57.5) * mm});
            skPoint(sketch, "E91.1.1.9", {"position": v(78.25, 57.5) * mm});
            skLineSegment(sketch, "E91.1.1.10", {"start": v(85.62, 32.5) * mm, "end": v(35.37, 32.5) * mm});
            skLineSegment(sketch, "E91.1.1.11", {"start": v(56.5, 37.5) * mm, "end": v(46.75, 37.5) * mm});
            skLineSegment(sketch, "E91.1.1.12", {"start": v(56.5, 52.5) * mm, "end": v(46.75, 52.5) * mm});
            skPoint(sketch, "E91.1.1.13", {"position": v(58.5, 72.5) * mm});
            skPoint(sketch, "E91.1.1.14", {"position": v(88.62, 52.5) * mm});
            skPoint(sketch, "E91.1.1.15", {"position": v(34.37, 72.5) * mm});
            skPoint(sketch, "E91.1.1.16", {"position": v(78.25, 52.5) * mm});
            skLineSegment(sketch, "E91.1.1.17", {"start": v(63.5, 52.5) * mm, "end": v(73.25, 52.5) * mm});
            skLineSegment(sketch, "E91.1.1.18", {"start": v(61.5, 59.5) * mm, "end": v(61.5, 70.5) * mm});
            skLineSegment(sketch, "E91.1.1.19", {"start": v(63.5, 57.5) * mm, "end": v(73.25, 57.5) * mm});
            skLineSegment(sketch, "E91.1.1.20", {"start": v(75.25, 59.5) * mm, "end": v(75.25, 70.5) * mm});
            skLineSegment(sketch, "E91.1.1.21", {"start": v(58.5, 59.5) * mm, "end": v(58.5, 70.5) * mm});
            skLineSegment(sketch, "E91.1.1.22", {"start": v(44.75, 59.5) * mm, "end": v(44.75, 70.5) * mm});
            skLineSegment(sketch, "E91.1.1.23", {"start": v(63.5, 72.5) * mm, "end": v(73.25, 72.5) * mm});
            skPoint(sketch, "E91.1.1.24", {"position": v(44.75, 57.5) * mm});
            skPoint(sketch, "E91.1.1.25", {"position": v(34.37, 52.5) * mm});
            skPoint(sketch, "E91.1.1.26", {"position": v(78.25, 37.5) * mm});
            skLineSegment(sketch, "E91.1.1.27", {"start": v(76.75, 91.36) * mm, "end": v(76.75, 21.84) * mm, "construction": true});
            skPoint(sketch, "E91.1.1.28", {"position": v(78.25, 72.5) * mm});
            skPoint(sketch, "E91.1.1.29", {"position": v(44.75, 52.5) * mm});
            skPoint(sketch, "E91.1.1.30", {"position": v(34.37, 32.5) * mm});
            skPoint(sketch, "E91.1.1.31", {"position": v(60, 55) * mm});
            skLineSegment(sketch, "E91.1.1.32", {"start": v(41.75, 50.5) * mm, "end": v(41.75, 39.5) * mm});
            skPoint(sketch, "E91.1.1.33", {"position": v(41.75, 37.5) * mm});
            skPoint(sketch, "E91.1.1.34", {"position": v(61.5, 52.5) * mm});
            skPoint(sketch, "E91.1.1.35", {"position": v(44.75, 37.5) * mm});
            skPoint(sketch, "E91.1.1.36", {"position": v(58.5, 37.5) * mm});
            skPoint(sketch, "E91.1.1.37", {"position": v(34.37, 37.5) * mm});
            skPoint(sketch, "E91.1.1.38", {"position": v(61.5, 37.5) * mm});
            skPoint(sketch, "E91.1.1.39", {"position": v(58.5, 52.5) * mm});
            skPoint(sketch, "E91.1.1.40", {"position": v(61.5, 72.5) * mm});
            skPoint(sketch, "E91.1.1.41", {"position": v(88.62, 37.5) * mm});
            skLineSegment(sketch, "E91.1.1.42", {"start": v(78.25, 50.5) * mm, "end": v(78.25, 39.5) * mm});
            skPoint(sketch, "E91.1.1.43", {"position": v(75.25, 52.5) * mm});
            skPoint(sketch, "E91.1.1.44", {"position": v(75.25, 57.5) * mm});
            skPoint(sketch, "E91.1.1.45", {"position": v(88.63, 32.5) * mm});
            skPoint(sketch, "E91.1.1.46", {"position": v(75.25, 37.5) * mm});
            skPoint(sketch, "E91.1.1.47", {"position": v(75.25, 72.5) * mm});
            skLineSegment(sketch, "E91.1.1.48", {"start": v(41.75, 59.5) * mm, "end": v(41.75, 70.5) * mm});
            skLineSegment(sketch, "E91.1.1.49", {"start": v(58.5, 50.5) * mm, "end": v(58.5, 39.5) * mm});
            skLineSegment(sketch, "E91.1.1.50", {"start": v(78.25, 59.5) * mm, "end": v(78.25, 70.5) * mm});
            skLineSegment(sketch, "E91.1.1.51", {"start": v(75.25, 50.5) * mm, "end": v(75.25, 39.5) * mm});
            skLineSegment(sketch, "E91.1.1.52", {"start": v(63.5, 37.5) * mm, "end": v(73.25, 37.5) * mm});
            skPoint(sketch, "E91.1.1.53", {"position": v(41.75, 72.5) * mm});
            skLineSegment(sketch, "E91.1.1.54", {"start": v(56.5, 57.5) * mm, "end": v(46.75, 57.5) * mm});
            skLineSegment(sketch, "E91.1.1.55", {"start": v(56.5, 72.5) * mm, "end": v(46.75, 72.5) * mm});
            skPoint(sketch, "E91.1.1.56", {"position": v(41.75, 52.5) * mm});
            skPoint(sketch, "E91.1.1.57", {"position": v(41.75, 57.5) * mm});
            skArc(sketch, "E91.1.1.58", {"start": v(58.5, 70.5) * mm, "mid": v(57.91, 71.91) * mm, "end": v(56.5, 72.5) * mm});
            skArc(sketch, "E91.1.1.59", {"start": v(61.5, 70.5) * mm, "mid": v(62.09, 71.91) * mm, "end": v(63.5, 72.5) * mm});
            skArc(sketch, "E91.1.1.60", {"start": v(58.5, 39.5) * mm, "mid": v(57.91, 38.09) * mm, "end": v(56.5, 37.5) * mm});
            skArc(sketch, "E91.1.1.61", {"start": v(56.5, 52.5) * mm, "mid": v(57.91, 51.91) * mm, "end": v(58.5, 50.5) * mm});
            skArc(sketch, "E91.1.1.62", {"start": v(46.75, 37.5) * mm, "mid": v(45.34, 38.09) * mm, "end": v(44.75, 39.5) * mm});
            skArc(sketch, "E91.1.1.63", {"start": v(35.38, 57.5) * mm, "mid": v(34.67, 57.2) * mm, "end": v(34.37, 56.5) * mm});
            skArc(sketch, "E91.1.1.64", {"start": v(46.75, 72.5) * mm, "mid": v(45.34, 71.91) * mm, "end": v(44.75, 70.5) * mm});
            skArc(sketch, "E91.1.1.65", {"start": v(56.5, 57.5) * mm, "mid": v(57.91, 58.09) * mm, "end": v(58.5, 59.5) * mm});
            skArc(sketch, "E91.1.1.66", {"start": v(73.25, 72.5) * mm, "mid": v(74.66, 71.91) * mm, "end": v(75.25, 70.5) * mm});
            skArc(sketch, "E91.1.1.67", {"start": v(63.5, 57.5) * mm, "mid": v(62.09, 58.09) * mm, "end": v(61.5, 59.5) * mm});
            skArc(sketch, "E91.1.1.68", {"start": v(39.75, 72.5) * mm, "mid": v(41.16, 71.91) * mm, "end": v(41.75, 70.5) * mm});
            skArc(sketch, "E91.1.1.69", {"start": v(39.75, 37.5) * mm, "mid": v(41.16, 38.09) * mm, "end": v(41.75, 39.5) * mm});
            skArc(sketch, "E91.1.1.70", {"start": v(80.25, 37.5) * mm, "mid": v(78.84, 38.09) * mm, "end": v(78.25, 39.5) * mm});
            skArc(sketch, "E91.1.1.71", {"start": v(75.25, 50.5) * mm, "mid": v(74.66, 51.91) * mm, "end": v(73.25, 52.5) * mm});
            skArc(sketch, "E91.1.1.72", {"start": v(80.25, 72.5) * mm, "mid": v(78.84, 71.91) * mm, "end": v(78.25, 70.5) * mm});
            skArc(sketch, "E91.1.1.73", {"start": v(44.75, 50.5) * mm, "mid": v(45.34, 51.91) * mm, "end": v(46.75, 52.5) * mm});
            skLineSegment(sketch, "E91.1.1.74", {"start": v(34.37, 76.5) * mm, "end": v(34.37, 73.5) * mm});
            skArc(sketch, "E91.1.1.75", {"start": v(78.25, 50.5) * mm, "mid": v(78.84, 51.91) * mm, "end": v(80.25, 52.5) * mm});
            skArc(sketch, "E91.1.1.76", {"start": v(73.25, 37.5) * mm, "mid": v(74.66, 38.09) * mm, "end": v(75.25, 39.5) * mm});
            skLineSegment(sketch, "E91.1.1.77", {"start": v(35.38, 57.5) * mm, "end": v(39.75, 57.5) * mm});
            skLineSegment(sketch, "E91.1.1.78", {"start": v(85.62, 52.5) * mm, "end": v(80.25, 52.5) * mm});
            skArc(sketch, "E91.1.1.79", {"start": v(63.5, 52.5) * mm, "mid": v(62.09, 51.91) * mm, "end": v(61.5, 50.5) * mm});
            skLineSegment(sketch, "E91.1.1.80", {"start": v(35.38, 72.5) * mm, "end": v(39.75, 72.5) * mm});
            skLineSegment(sketch, "E91.1.1.81", {"start": v(85.62, 72.5) * mm, "end": v(80.25, 72.5) * mm});
            skArc(sketch, "E91.1.1.82", {"start": v(61.5, 39.5) * mm, "mid": v(62.09, 38.09) * mm, "end": v(63.5, 37.5) * mm});
            skLineSegment(sketch, "E91.1.1.83", {"start": v(85.62, 37.5) * mm, "end": v(80.25, 37.5) * mm});
            skArc(sketch, "E91.1.1.84", {"start": v(35.38, 77.5) * mm, "mid": v(34.67, 77.2) * mm, "end": v(34.37, 76.5) * mm});
            skArc(sketch, "E91.1.1.85", {"start": v(34.37, 73.5) * mm, "mid": v(34.67, 72.8) * mm, "end": v(35.38, 72.5) * mm});
            skLineSegment(sketch, "E91.1.1.86", {"start": v(34.37, 56.5) * mm, "end": v(34.37, 53.5) * mm});
            skArc(sketch, "E91.1.1.87", {"start": v(34.37, 33.5) * mm, "mid": v(34.67, 32.8) * mm, "end": v(35.38, 32.5) * mm});
            skLineSegment(sketch, "E91.1.1.88", {"start": v(34.37, 36.5) * mm, "end": v(34.37, 33.5) * mm});
            skArc(sketch, "E91.1.1.89", {"start": v(34.37, 53.5) * mm, "mid": v(34.67, 52.8) * mm, "end": v(35.38, 52.5) * mm});
            skArc(sketch, "E91.1.1.90", {"start": v(35.38, 37.5) * mm, "mid": v(34.67, 37.2) * mm, "end": v(34.37, 36.5) * mm});
            skArc(sketch, "E91.1.1.91", {"start": v(41.75, 59.5) * mm, "mid": v(41.16, 58.09) * mm, "end": v(39.75, 57.5) * mm});
            skArc(sketch, "E91.1.1.92", {"start": v(41.75, 50.5) * mm, "mid": v(41.16, 51.91) * mm, "end": v(39.75, 52.5) * mm});
            skArc(sketch, "E91.1.1.93", {"start": v(44.75, 59.5) * mm, "mid": v(45.34, 58.09) * mm, "end": v(46.75, 57.5) * mm});
            skArc(sketch, "E91.1.1.94", {"start": v(75.25, 59.5) * mm, "mid": v(74.66, 58.09) * mm, "end": v(73.25, 57.5) * mm});
            skLineSegment(sketch, "E91.1.1.95", {"start": v(35.38, 52.5) * mm, "end": v(39.75, 52.5) * mm});
            skLineSegment(sketch, "E91.1.1.96", {"start": v(35.38, 37.5) * mm, "end": v(39.75, 37.5) * mm});
            skLineSegment(sketch, "E91.1.1.97", {"start": v(85.62, 57.5) * mm, "end": v(80.25, 57.5) * mm});
            skLineSegment(sketch, "E91.1.1.98", {"start": v(85.62, 37.5) * mm, "end": v(85.62, 32.5) * mm});
            skLineSegment(sketch, "E91.1.1.99", {"start": v(85.62, 77.5) * mm, "end": v(87.63, 77.5) * mm});
            skLineSegment(sketch, "E91.1.1.100", {"start": v(85.62, 72.5) * mm, "end": v(87.63, 72.5) * mm});
            skArc(sketch, "E91.1.1.101", {"start": v(88.63, 36.5) * mm, "mid": v(88.33, 37.2) * mm, "end": v(87.63, 37.5) * mm});
            skLineSegment(sketch, "E91.1.1.102", {"start": v(85.62, 77.5) * mm, "end": v(85.62, 72.5) * mm});
            skArc(sketch, "E91.1.1.103", {"start": v(87.63, 32.5) * mm, "mid": v(88.33, 32.8) * mm, "end": v(88.63, 33.5) * mm});
            skLineSegment(sketch, "E91.1.1.104", {"start": v(88.62, 76.5) * mm, "end": v(88.62, 73.5) * mm});
            skArc(sketch, "E91.1.1.105", {"start": v(88.63, 56.5) * mm, "mid": v(88.33, 57.2) * mm, "end": v(87.63, 57.5) * mm});
            skLineSegment(sketch, "E91.1.1.106", {"start": v(85.62, 57.5) * mm, "end": v(87.63, 57.5) * mm});
            skArc(sketch, "E91.1.1.107", {"start": v(78.25, 59.5) * mm, "mid": v(78.84, 58.09) * mm, "end": v(80.25, 57.5) * mm});
            skArc(sketch, "E91.1.1.108", {"start": v(87.63, 72.5) * mm, "mid": v(88.33, 72.8) * mm, "end": v(88.63, 73.5) * mm});
            skArc(sketch, "E91.1.1.109", {"start": v(88.63, 76.5) * mm, "mid": v(88.33, 77.2) * mm, "end": v(87.63, 77.5) * mm});
            skLineSegment(sketch, "E91.1.1.110", {"start": v(85.62, 37.5) * mm, "end": v(87.63, 37.5) * mm});
            skLineSegment(sketch, "E91.1.1.111", {"start": v(85.62, 32.5) * mm, "end": v(87.63, 32.5) * mm});
            skLineSegment(sketch, "E91.1.1.112", {"start": v(88.63, 36.5) * mm, "end": v(88.63, 33.5) * mm});
            skLineSegment(sketch, "E91.1.1.113", {"start": v(85.62, 77.5) * mm, "end": v(85.62, 72.5) * mm});
            skArc(sketch, "E91.1.1.114", {"start": v(87.63, 52.5) * mm, "mid": v(88.33, 52.8) * mm, "end": v(88.63, 53.5) * mm});
            skLineSegment(sketch, "E91.1.1.115", {"start": v(85.62, 52.5) * mm, "end": v(87.63, 52.5) * mm});
            skLineSegment(sketch, "E91.1.1.116", {"start": v(88.62, 56.5) * mm, "end": v(88.62, 53.5) * mm});
            skLineSegment(sketch, "E91.1.1.117", {"start": v(85.62, 37.5) * mm, "end": v(85.62, 32.5) * mm});
            skLineSegment(sketch, "E91.1.1.118", {"start": v(85.62, 57.5) * mm, "end": v(85.62, 52.5) * mm});
            skLineSegment(sketch, "E91.1.1.119", {"start": v(85.62, 57.5) * mm, "end": v(85.62, 52.5) * mm});
            skPoint(sketch, "E91.2.0.0", {"position": v(104.75, 17.5) * mm});
            skPoint(sketch, "E91.2.0.1", {"position": v(121.5, 2.5) * mm});
            skPoint(sketch, "E91.2.0.2", {"position": v(148.62, 2.5) * mm});
            skLineSegment(sketch, "E91.2.0.3", {"start": v(145.62, 22.5) * mm, "end": v(95.38, 22.5) * mm});
            skLineSegment(sketch, "E91.2.0.4", {"start": v(104.75, -4.5) * mm, "end": v(104.75, -15.5) * mm});
            skLineSegment(sketch, "E91.2.0.5", {"start": v(121.5, -4.5) * mm, "end": v(121.5, -15.5) * mm});
            skPoint(sketch, "E91.2.0.6", {"position": v(118.5, 2.5) * mm});
            skPoint(sketch, "E91.2.0.7", {"position": v(148.62, 17.5) * mm});
            skPoint(sketch, "E91.2.0.8", {"position": v(94.37, 2.5) * mm});
            skPoint(sketch, "E91.2.0.9", {"position": v(138.25, 2.5) * mm});
            skLineSegment(sketch, "E91.2.0.10", {"start": v(145.62, -22.5) * mm, "end": v(95.37, -22.5) * mm});
            skLineSegment(sketch, "E91.2.0.11", {"start": v(116.5, -17.5) * mm, "end": v(106.75, -17.5) * mm});
            skLineSegment(sketch, "E91.2.0.12", {"start": v(116.5, -2.5) * mm, "end": v(106.75, -2.5) * mm});
            skPoint(sketch, "E91.2.0.13", {"position": v(118.5, 17.5) * mm});
            skPoint(sketch, "E91.2.0.14", {"position": v(148.62, -2.5) * mm});
            skPoint(sketch, "E91.2.0.15", {"position": v(94.37, 17.5) * mm});
            skPoint(sketch, "E91.2.0.16", {"position": v(138.25, -2.5) * mm});
            skLineSegment(sketch, "E91.2.0.17", {"start": v(123.5, -2.5) * mm, "end": v(133.25, -2.5) * mm});
            skLineSegment(sketch, "E91.2.0.18", {"start": v(121.5, 4.5) * mm, "end": v(121.5, 15.5) * mm});
            skLineSegment(sketch, "E91.2.0.19", {"start": v(123.5, 2.5) * mm, "end": v(133.25, 2.5) * mm});
            skLineSegment(sketch, "E91.2.0.20", {"start": v(135.25, 4.5) * mm, "end": v(135.25, 15.5) * mm});
            skLineSegment(sketch, "E91.2.0.21", {"start": v(118.5, 4.5) * mm, "end": v(118.5, 15.5) * mm});
            skLineSegment(sketch, "E91.2.0.22", {"start": v(104.75, 4.5) * mm, "end": v(104.75, 15.5) * mm});
            skLineSegment(sketch, "E91.2.0.23", {"start": v(123.5, 17.5) * mm, "end": v(133.25, 17.5) * mm});
            skPoint(sketch, "E91.2.0.24", {"position": v(104.75, 2.5) * mm});
            skPoint(sketch, "E91.2.0.25", {"position": v(94.37, -2.5) * mm});
            skPoint(sketch, "E91.2.0.26", {"position": v(138.25, -17.5) * mm});
            skLineSegment(sketch, "E91.2.0.27", {"start": v(136.75, 36.36) * mm, "end": v(136.75, -33.16) * mm, "construction": true});
            skPoint(sketch, "E91.2.0.28", {"position": v(138.25, 17.5) * mm});
            skPoint(sketch, "E91.2.0.29", {"position": v(104.75, -2.5) * mm});
            skPoint(sketch, "E91.2.0.30", {"position": v(94.37, -22.5) * mm});
            skPoint(sketch, "E91.2.0.31", {"position": v(120, 0) * mm});
            skLineSegment(sketch, "E91.2.0.32", {"start": v(101.75, -4.5) * mm, "end": v(101.75, -15.5) * mm});
            skPoint(sketch, "E91.2.0.33", {"position": v(101.75, -17.5) * mm});
            skPoint(sketch, "E91.2.0.34", {"position": v(121.5, -2.5) * mm});
            skPoint(sketch, "E91.2.0.35", {"position": v(104.75, -17.5) * mm});
            skPoint(sketch, "E91.2.0.36", {"position": v(118.5, -17.5) * mm});
            skPoint(sketch, "E91.2.0.37", {"position": v(94.37, -17.5) * mm});
            skPoint(sketch, "E91.2.0.38", {"position": v(121.5, -17.5) * mm});
            skPoint(sketch, "E91.2.0.39", {"position": v(118.5, -2.5) * mm});
            skPoint(sketch, "E91.2.0.40", {"position": v(121.5, 17.5) * mm});
            skPoint(sketch, "E91.2.0.41", {"position": v(148.62, -17.5) * mm});
            skLineSegment(sketch, "E91.2.0.42", {"start": v(138.25, -4.5) * mm, "end": v(138.25, -15.5) * mm});
            skPoint(sketch, "E91.2.0.43", {"position": v(135.25, -2.5) * mm});
            skPoint(sketch, "E91.2.0.44", {"position": v(135.25, 2.5) * mm});
            skPoint(sketch, "E91.2.0.45", {"position": v(148.62, -22.5) * mm});
            skPoint(sketch, "E91.2.0.46", {"position": v(135.25, -17.5) * mm});
            skPoint(sketch, "E91.2.0.47", {"position": v(135.25, 17.5) * mm});
            skLineSegment(sketch, "E91.2.0.48", {"start": v(101.75, 4.5) * mm, "end": v(101.75, 15.5) * mm});
            skLineSegment(sketch, "E91.2.0.49", {"start": v(118.5, -4.5) * mm, "end": v(118.5, -15.5) * mm});
            skLineSegment(sketch, "E91.2.0.50", {"start": v(138.25, 4.5) * mm, "end": v(138.25, 15.5) * mm});
            skLineSegment(sketch, "E91.2.0.51", {"start": v(135.25, -4.5) * mm, "end": v(135.25, -15.5) * mm});
            skLineSegment(sketch, "E91.2.0.52", {"start": v(123.5, -17.5) * mm, "end": v(133.25, -17.5) * mm});
            skPoint(sketch, "E91.2.0.53", {"position": v(101.75, 17.5) * mm});
            skLineSegment(sketch, "E91.2.0.54", {"start": v(116.5, 2.5) * mm, "end": v(106.75, 2.5) * mm});
            skLineSegment(sketch, "E91.2.0.55", {"start": v(116.5, 17.5) * mm, "end": v(106.75, 17.5) * mm});
            skPoint(sketch, "E91.2.0.56", {"position": v(101.75, -2.5) * mm});
            skPoint(sketch, "E91.2.0.57", {"position": v(101.75, 2.5) * mm});
            skArc(sketch, "E91.2.0.58", {"start": v(118.5, 15.5) * mm, "mid": v(117.91, 16.91) * mm, "end": v(116.5, 17.5) * mm});
            skArc(sketch, "E91.2.0.59", {"start": v(121.5, 15.5) * mm, "mid": v(122.09, 16.91) * mm, "end": v(123.5, 17.5) * mm});
            skArc(sketch, "E91.2.0.60", {"start": v(118.5, -15.5) * mm, "mid": v(117.91, -16.91) * mm, "end": v(116.5, -17.5) * mm});
            skArc(sketch, "E91.2.0.61", {"start": v(116.5, -2.5) * mm, "mid": v(117.91, -3.09) * mm, "end": v(118.5, -4.5) * mm});
            skArc(sketch, "E91.2.0.62", {"start": v(106.75, -17.5) * mm, "mid": v(105.34, -16.91) * mm, "end": v(104.75, -15.5) * mm});
            skArc(sketch, "E91.2.0.63", {"start": v(95.37, 2.5) * mm, "mid": v(94.67, 2.2) * mm, "end": v(94.37, 1.5) * mm});
            skArc(sketch, "E91.2.0.64", {"start": v(106.75, 17.5) * mm, "mid": v(105.34, 16.91) * mm, "end": v(104.75, 15.5) * mm});
            skArc(sketch, "E91.2.0.65", {"start": v(116.5, 2.5) * mm, "mid": v(117.91, 3.09) * mm, "end": v(118.5, 4.5) * mm});
            skArc(sketch, "E91.2.0.66", {"start": v(133.25, 17.5) * mm, "mid": v(134.66, 16.91) * mm, "end": v(135.25, 15.5) * mm});
            skArc(sketch, "E91.2.0.67", {"start": v(123.5, 2.5) * mm, "mid": v(122.09, 3.09) * mm, "end": v(121.5, 4.5) * mm});
            skArc(sketch, "E91.2.0.68", {"start": v(99.75, 17.5) * mm, "mid": v(101.16, 16.91) * mm, "end": v(101.75, 15.5) * mm});
            skArc(sketch, "E91.2.0.69", {"start": v(99.75, -17.5) * mm, "mid": v(101.16, -16.91) * mm, "end": v(101.75, -15.5) * mm});
            skArc(sketch, "E91.2.0.70", {"start": v(140.25, -17.5) * mm, "mid": v(138.84, -16.91) * mm, "end": v(138.25, -15.5) * mm});
            skArc(sketch, "E91.2.0.71", {"start": v(135.25, -4.5) * mm, "mid": v(134.66, -3.09) * mm, "end": v(133.25, -2.5) * mm});
            skArc(sketch, "E91.2.0.72", {"start": v(140.25, 17.5) * mm, "mid": v(138.84, 16.91) * mm, "end": v(138.25, 15.5) * mm});
            skArc(sketch, "E91.2.0.73", {"start": v(104.75, -4.5) * mm, "mid": v(105.34, -3.09) * mm, "end": v(106.75, -2.5) * mm});
            skLineSegment(sketch, "E91.2.0.74", {"start": v(94.37, 21.5) * mm, "end": v(94.37, 18.5) * mm});
            skArc(sketch, "E91.2.0.75", {"start": v(138.25, -4.5) * mm, "mid": v(138.84, -3.09) * mm, "end": v(140.25, -2.5) * mm});
            skArc(sketch, "E91.2.0.76", {"start": v(133.25, -17.5) * mm, "mid": v(134.66, -16.91) * mm, "end": v(135.25, -15.5) * mm});
            skLineSegment(sketch, "E91.2.0.77", {"start": v(95.37, 2.5) * mm, "end": v(99.75, 2.5) * mm});
            skLineSegment(sketch, "E91.2.0.78", {"start": v(145.62, -2.5) * mm, "end": v(140.25, -2.5) * mm});
            skArc(sketch, "E91.2.0.79", {"start": v(123.5, -2.5) * mm, "mid": v(122.09, -3.09) * mm, "end": v(121.5, -4.5) * mm});
            skLineSegment(sketch, "E91.2.0.80", {"start": v(95.37, 17.5) * mm, "end": v(99.75, 17.5) * mm});
            skLineSegment(sketch, "E91.2.0.81", {"start": v(145.62, 17.5) * mm, "end": v(140.25, 17.5) * mm});
            skArc(sketch, "E91.2.0.82", {"start": v(121.5, -15.5) * mm, "mid": v(122.09, -16.91) * mm, "end": v(123.5, -17.5) * mm});
            skLineSegment(sketch, "E91.2.0.83", {"start": v(145.62, -17.5) * mm, "end": v(140.25, -17.5) * mm});
            skArc(sketch, "E91.2.0.84", {"start": v(95.37, 22.5) * mm, "mid": v(94.67, 22.2) * mm, "end": v(94.37, 21.5) * mm});
            skArc(sketch, "E91.2.0.85", {"start": v(94.37, 18.5) * mm, "mid": v(94.67, 17.8) * mm, "end": v(95.37, 17.5) * mm});
            skLineSegment(sketch, "E91.2.0.86", {"start": v(94.37, 1.5) * mm, "end": v(94.37, -1.5) * mm});
            skArc(sketch, "E91.2.0.87", {"start": v(94.37, -21.5) * mm, "mid": v(94.67, -22.2) * mm, "end": v(95.37, -22.5) * mm});
            skLineSegment(sketch, "E91.2.0.88", {"start": v(94.37, -18.5) * mm, "end": v(94.37, -21.5) * mm});
            skArc(sketch, "E91.2.0.89", {"start": v(94.37, -1.5) * mm, "mid": v(94.67, -2.2) * mm, "end": v(95.37, -2.5) * mm});
            skArc(sketch, "E91.2.0.90", {"start": v(95.37, -17.5) * mm, "mid": v(94.67, -17.8) * mm, "end": v(94.37, -18.5) * mm});
            skArc(sketch, "E91.2.0.91", {"start": v(101.75, 4.5) * mm, "mid": v(101.16, 3.09) * mm, "end": v(99.75, 2.5) * mm});
            skArc(sketch, "E91.2.0.92", {"start": v(101.75, -4.5) * mm, "mid": v(101.16, -3.09) * mm, "end": v(99.75, -2.5) * mm});
            skArc(sketch, "E91.2.0.93", {"start": v(104.75, 4.5) * mm, "mid": v(105.34, 3.09) * mm, "end": v(106.75, 2.5) * mm});
            skArc(sketch, "E91.2.0.94", {"start": v(135.25, 4.5) * mm, "mid": v(134.66, 3.09) * mm, "end": v(133.25, 2.5) * mm});
            skLineSegment(sketch, "E91.2.0.95", {"start": v(95.37, -2.5) * mm, "end": v(99.75, -2.5) * mm});
            skLineSegment(sketch, "E91.2.0.96", {"start": v(95.37, -17.5) * mm, "end": v(99.75, -17.5) * mm});
            skLineSegment(sketch, "E91.2.0.97", {"start": v(145.62, 2.5) * mm, "end": v(140.25, 2.5) * mm});
            skLineSegment(sketch, "E91.2.0.98", {"start": v(145.62, -17.5) * mm, "end": v(145.62, -22.5) * mm});
            skLineSegment(sketch, "E91.2.0.99", {"start": v(145.62, 22.5) * mm, "end": v(147.62, 22.5) * mm});
            skLineSegment(sketch, "E91.2.0.100", {"start": v(145.62, 17.5) * mm, "end": v(147.62, 17.5) * mm});
            skArc(sketch, "E91.2.0.101", {"start": v(148.62, -18.5) * mm, "mid": v(148.33, -17.8) * mm, "end": v(147.62, -17.5) * mm});
            skLineSegment(sketch, "E91.2.0.102", {"start": v(145.62, 22.5) * mm, "end": v(145.62, 17.5) * mm});
            skArc(sketch, "E91.2.0.103", {"start": v(147.62, -22.5) * mm, "mid": v(148.33, -22.2) * mm, "end": v(148.62, -21.5) * mm});
            skLineSegment(sketch, "E91.2.0.104", {"start": v(148.62, 21.5) * mm, "end": v(148.62, 18.5) * mm});
            skArc(sketch, "E91.2.0.105", {"start": v(148.62, 1.5) * mm, "mid": v(148.33, 2.2) * mm, "end": v(147.62, 2.5) * mm});
            skLineSegment(sketch, "E91.2.0.106", {"start": v(145.62, 2.5) * mm, "end": v(147.62, 2.5) * mm});
            skArc(sketch, "E91.2.0.107", {"start": v(138.25, 4.5) * mm, "mid": v(138.84, 3.09) * mm, "end": v(140.25, 2.5) * mm});
            skArc(sketch, "E91.2.0.108", {"start": v(147.62, 17.5) * mm, "mid": v(148.33, 17.8) * mm, "end": v(148.62, 18.5) * mm});
            skArc(sketch, "E91.2.0.109", {"start": v(148.62, 21.5) * mm, "mid": v(148.33, 22.2) * mm, "end": v(147.62, 22.5) * mm});
            skLineSegment(sketch, "E91.2.0.110", {"start": v(145.62, -17.5) * mm, "end": v(147.62, -17.5) * mm});
            skLineSegment(sketch, "E91.2.0.111", {"start": v(145.62, -22.5) * mm, "end": v(147.62, -22.5) * mm});
            skLineSegment(sketch, "E91.2.0.112", {"start": v(148.62, -18.5) * mm, "end": v(148.62, -21.5) * mm});
            skLineSegment(sketch, "E91.2.0.113", {"start": v(145.62, 22.5) * mm, "end": v(145.62, 17.5) * mm});
            skArc(sketch, "E91.2.0.114", {"start": v(147.62, -2.5) * mm, "mid": v(148.33, -2.2) * mm, "end": v(148.62, -1.5) * mm});
            skLineSegment(sketch, "E91.2.0.115", {"start": v(145.62, -2.5) * mm, "end": v(147.62, -2.5) * mm});
            skLineSegment(sketch, "E91.2.0.116", {"start": v(148.62, 1.5) * mm, "end": v(148.62, -1.5) * mm});
            skLineSegment(sketch, "E91.2.0.117", {"start": v(145.62, -17.5) * mm, "end": v(145.62, -22.5) * mm});
            skLineSegment(sketch, "E91.2.0.118", {"start": v(145.62, 2.5) * mm, "end": v(145.62, -2.5) * mm});
            skLineSegment(sketch, "E91.2.0.119", {"start": v(145.62, 2.5) * mm, "end": v(145.62, -2.5) * mm});
            skPoint(sketch, "E91.2.1.0", {"position": v(104.75, 72.5) * mm});
            skPoint(sketch, "E91.2.1.1", {"position": v(121.5, 57.5) * mm});
            skPoint(sketch, "E91.2.1.2", {"position": v(148.62, 57.5) * mm});
            skLineSegment(sketch, "E91.2.1.3", {"start": v(145.62, 77.5) * mm, "end": v(95.38, 77.5) * mm});
            skLineSegment(sketch, "E91.2.1.4", {"start": v(104.75, 50.5) * mm, "end": v(104.75, 39.5) * mm});
            skLineSegment(sketch, "E91.2.1.5", {"start": v(121.5, 50.5) * mm, "end": v(121.5, 39.5) * mm});
            skPoint(sketch, "E91.2.1.6", {"position": v(118.5, 57.5) * mm});
            skPoint(sketch, "E91.2.1.7", {"position": v(148.62, 72.5) * mm});
            skPoint(sketch, "E91.2.1.8", {"position": v(94.37, 57.5) * mm});
            skPoint(sketch, "E91.2.1.9", {"position": v(138.25, 57.5) * mm});
            skLineSegment(sketch, "E91.2.1.10", {"start": v(145.62, 32.5) * mm, "end": v(95.37, 32.5) * mm});
            skLineSegment(sketch, "E91.2.1.11", {"start": v(116.5, 37.5) * mm, "end": v(106.75, 37.5) * mm});
            skLineSegment(sketch, "E91.2.1.12", {"start": v(116.5, 52.5) * mm, "end": v(106.75, 52.5) * mm});
            skPoint(sketch, "E91.2.1.13", {"position": v(118.5, 72.5) * mm});
            skPoint(sketch, "E91.2.1.14", {"position": v(148.62, 52.5) * mm});
            skPoint(sketch, "E91.2.1.15", {"position": v(94.37, 72.5) * mm});
            skPoint(sketch, "E91.2.1.16", {"position": v(138.25, 52.5) * mm});
            skLineSegment(sketch, "E91.2.1.17", {"start": v(123.5, 52.5) * mm, "end": v(133.25, 52.5) * mm});
            skLineSegment(sketch, "E91.2.1.18", {"start": v(121.5, 59.5) * mm, "end": v(121.5, 70.5) * mm});
            skLineSegment(sketch, "E91.2.1.19", {"start": v(123.5, 57.5) * mm, "end": v(133.25, 57.5) * mm});
            skLineSegment(sketch, "E91.2.1.20", {"start": v(135.25, 59.5) * mm, "end": v(135.25, 70.5) * mm});
            skLineSegment(sketch, "E91.2.1.21", {"start": v(118.5, 59.5) * mm, "end": v(118.5, 70.5) * mm});
            skLineSegment(sketch, "E91.2.1.22", {"start": v(104.75, 59.5) * mm, "end": v(104.75, 70.5) * mm});
            skLineSegment(sketch, "E91.2.1.23", {"start": v(123.5, 72.5) * mm, "end": v(133.25, 72.5) * mm});
            skPoint(sketch, "E91.2.1.24", {"position": v(104.75, 57.5) * mm});
            skPoint(sketch, "E91.2.1.25", {"position": v(94.37, 52.5) * mm});
            skPoint(sketch, "E91.2.1.26", {"position": v(138.25, 37.5) * mm});
            skLineSegment(sketch, "E91.2.1.27", {"start": v(136.75, 91.36) * mm, "end": v(136.75, 21.84) * mm, "construction": true});
            skPoint(sketch, "E91.2.1.28", {"position": v(138.25, 72.5) * mm});
            skPoint(sketch, "E91.2.1.29", {"position": v(104.75, 52.5) * mm});
            skPoint(sketch, "E91.2.1.30", {"position": v(94.37, 32.5) * mm});
            skPoint(sketch, "E91.2.1.31", {"position": v(120, 55) * mm});
            skLineSegment(sketch, "E91.2.1.32", {"start": v(101.75, 50.5) * mm, "end": v(101.75, 39.5) * mm});
            skPoint(sketch, "E91.2.1.33", {"position": v(101.75, 37.5) * mm});
            skPoint(sketch, "E91.2.1.34", {"position": v(121.5, 52.5) * mm});
            skPoint(sketch, "E91.2.1.35", {"position": v(104.75, 37.5) * mm});
            skPoint(sketch, "E91.2.1.36", {"position": v(118.5, 37.5) * mm});
            skPoint(sketch, "E91.2.1.37", {"position": v(94.37, 37.5) * mm});
            skPoint(sketch, "E91.2.1.38", {"position": v(121.5, 37.5) * mm});
            skPoint(sketch, "E91.2.1.39", {"position": v(118.5, 52.5) * mm});
            skPoint(sketch, "E91.2.1.40", {"position": v(121.5, 72.5) * mm});
            skPoint(sketch, "E91.2.1.41", {"position": v(148.62, 37.5) * mm});
            skLineSegment(sketch, "E91.2.1.42", {"start": v(138.25, 50.5) * mm, "end": v(138.25, 39.5) * mm});
            skPoint(sketch, "E91.2.1.43", {"position": v(135.25, 52.5) * mm});
            skPoint(sketch, "E91.2.1.44", {"position": v(135.25, 57.5) * mm});
            skPoint(sketch, "E91.2.1.45", {"position": v(148.62, 32.5) * mm});
            skPoint(sketch, "E91.2.1.46", {"position": v(135.25, 37.5) * mm});
            skPoint(sketch, "E91.2.1.47", {"position": v(135.25, 72.5) * mm});
            skLineSegment(sketch, "E91.2.1.48", {"start": v(101.75, 59.5) * mm, "end": v(101.75, 70.5) * mm});
            skLineSegment(sketch, "E91.2.1.49", {"start": v(118.5, 50.5) * mm, "end": v(118.5, 39.5) * mm});
            skLineSegment(sketch, "E91.2.1.50", {"start": v(138.25, 59.5) * mm, "end": v(138.25, 70.5) * mm});
            skLineSegment(sketch, "E91.2.1.51", {"start": v(135.25, 50.5) * mm, "end": v(135.25, 39.5) * mm});
            skLineSegment(sketch, "E91.2.1.52", {"start": v(123.5, 37.5) * mm, "end": v(133.25, 37.5) * mm});
            skPoint(sketch, "E91.2.1.53", {"position": v(101.75, 72.5) * mm});
            skLineSegment(sketch, "E91.2.1.54", {"start": v(116.5, 57.5) * mm, "end": v(106.75, 57.5) * mm});
            skLineSegment(sketch, "E91.2.1.55", {"start": v(116.5, 72.5) * mm, "end": v(106.75, 72.5) * mm});
            skPoint(sketch, "E91.2.1.56", {"position": v(101.75, 52.5) * mm});
            skPoint(sketch, "E91.2.1.57", {"position": v(101.75, 57.5) * mm});
            skArc(sketch, "E91.2.1.58", {"start": v(118.5, 70.5) * mm, "mid": v(117.91, 71.91) * mm, "end": v(116.5, 72.5) * mm});
            skArc(sketch, "E91.2.1.59", {"start": v(121.5, 70.5) * mm, "mid": v(122.09, 71.91) * mm, "end": v(123.5, 72.5) * mm});
            skArc(sketch, "E91.2.1.60", {"start": v(118.5, 39.5) * mm, "mid": v(117.91, 38.09) * mm, "end": v(116.5, 37.5) * mm});
            skArc(sketch, "E91.2.1.61", {"start": v(116.5, 52.5) * mm, "mid": v(117.91, 51.91) * mm, "end": v(118.5, 50.5) * mm});
            skArc(sketch, "E91.2.1.62", {"start": v(106.75, 37.5) * mm, "mid": v(105.34, 38.09) * mm, "end": v(104.75, 39.5) * mm});
            skArc(sketch, "E91.2.1.63", {"start": v(95.37, 57.5) * mm, "mid": v(94.67, 57.2) * mm, "end": v(94.37, 56.5) * mm});
            skArc(sketch, "E91.2.1.64", {"start": v(106.75, 72.5) * mm, "mid": v(105.34, 71.91) * mm, "end": v(104.75, 70.5) * mm});
            skArc(sketch, "E91.2.1.65", {"start": v(116.5, 57.5) * mm, "mid": v(117.91, 58.09) * mm, "end": v(118.5, 59.5) * mm});
            skArc(sketch, "E91.2.1.66", {"start": v(133.25, 72.5) * mm, "mid": v(134.66, 71.91) * mm, "end": v(135.25, 70.5) * mm});
            skArc(sketch, "E91.2.1.67", {"start": v(123.5, 57.5) * mm, "mid": v(122.09, 58.09) * mm, "end": v(121.5, 59.5) * mm});
            skArc(sketch, "E91.2.1.68", {"start": v(99.75, 72.5) * mm, "mid": v(101.16, 71.91) * mm, "end": v(101.75, 70.5) * mm});
            skArc(sketch, "E91.2.1.69", {"start": v(99.75, 37.5) * mm, "mid": v(101.16, 38.09) * mm, "end": v(101.75, 39.5) * mm});
            skArc(sketch, "E91.2.1.70", {"start": v(140.25, 37.5) * mm, "mid": v(138.84, 38.09) * mm, "end": v(138.25, 39.5) * mm});
            skArc(sketch, "E91.2.1.71", {"start": v(135.25, 50.5) * mm, "mid": v(134.66, 51.91) * mm, "end": v(133.25, 52.5) * mm});
            skArc(sketch, "E91.2.1.72", {"start": v(140.25, 72.5) * mm, "mid": v(138.84, 71.91) * mm, "end": v(138.25, 70.5) * mm});
            skArc(sketch, "E91.2.1.73", {"start": v(104.75, 50.5) * mm, "mid": v(105.34, 51.91) * mm, "end": v(106.75, 52.5) * mm});
            skLineSegment(sketch, "E91.2.1.74", {"start": v(94.37, 76.5) * mm, "end": v(94.37, 73.5) * mm});
            skArc(sketch, "E91.2.1.75", {"start": v(138.25, 50.5) * mm, "mid": v(138.84, 51.91) * mm, "end": v(140.25, 52.5) * mm});
            skArc(sketch, "E91.2.1.76", {"start": v(133.25, 37.5) * mm, "mid": v(134.66, 38.09) * mm, "end": v(135.25, 39.5) * mm});
            skLineSegment(sketch, "E91.2.1.77", {"start": v(95.37, 57.5) * mm, "end": v(99.75, 57.5) * mm});
            skLineSegment(sketch, "E91.2.1.78", {"start": v(145.62, 52.5) * mm, "end": v(140.25, 52.5) * mm});
            skArc(sketch, "E91.2.1.79", {"start": v(123.5, 52.5) * mm, "mid": v(122.09, 51.91) * mm, "end": v(121.5, 50.5) * mm});
            skLineSegment(sketch, "E91.2.1.80", {"start": v(95.37, 72.5) * mm, "end": v(99.75, 72.5) * mm});
            skLineSegment(sketch, "E91.2.1.81", {"start": v(145.62, 72.5) * mm, "end": v(140.25, 72.5) * mm});
            skArc(sketch, "E91.2.1.82", {"start": v(121.5, 39.5) * mm, "mid": v(122.09, 38.09) * mm, "end": v(123.5, 37.5) * mm});
            skLineSegment(sketch, "E91.2.1.83", {"start": v(145.62, 37.5) * mm, "end": v(140.25, 37.5) * mm});
            skArc(sketch, "E91.2.1.84", {"start": v(95.37, 77.5) * mm, "mid": v(94.67, 77.2) * mm, "end": v(94.37, 76.5) * mm});
            skArc(sketch, "E91.2.1.85", {"start": v(94.37, 73.5) * mm, "mid": v(94.67, 72.8) * mm, "end": v(95.37, 72.5) * mm});
            skLineSegment(sketch, "E91.2.1.86", {"start": v(94.37, 56.5) * mm, "end": v(94.37, 53.5) * mm});
            skArc(sketch, "E91.2.1.87", {"start": v(94.37, 33.5) * mm, "mid": v(94.67, 32.8) * mm, "end": v(95.37, 32.5) * mm});
            skLineSegment(sketch, "E91.2.1.88", {"start": v(94.37, 36.5) * mm, "end": v(94.37, 33.5) * mm});
            skArc(sketch, "E91.2.1.89", {"start": v(94.37, 53.5) * mm, "mid": v(94.67, 52.8) * mm, "end": v(95.37, 52.5) * mm});
            skArc(sketch, "E91.2.1.90", {"start": v(95.37, 37.5) * mm, "mid": v(94.67, 37.2) * mm, "end": v(94.37, 36.5) * mm});
            skArc(sketch, "E91.2.1.91", {"start": v(101.75, 59.5) * mm, "mid": v(101.16, 58.09) * mm, "end": v(99.75, 57.5) * mm});
            skArc(sketch, "E91.2.1.92", {"start": v(101.75, 50.5) * mm, "mid": v(101.16, 51.91) * mm, "end": v(99.75, 52.5) * mm});
            skArc(sketch, "E91.2.1.93", {"start": v(104.75, 59.5) * mm, "mid": v(105.34, 58.09) * mm, "end": v(106.75, 57.5) * mm});
            skArc(sketch, "E91.2.1.94", {"start": v(135.25, 59.5) * mm, "mid": v(134.66, 58.09) * mm, "end": v(133.25, 57.5) * mm});
            skLineSegment(sketch, "E91.2.1.95", {"start": v(95.37, 52.5) * mm, "end": v(99.75, 52.5) * mm});
            skLineSegment(sketch, "E91.2.1.96", {"start": v(95.37, 37.5) * mm, "end": v(99.75, 37.5) * mm});
            skLineSegment(sketch, "E91.2.1.97", {"start": v(145.62, 57.5) * mm, "end": v(140.25, 57.5) * mm});
            skLineSegment(sketch, "E91.2.1.98", {"start": v(145.62, 37.5) * mm, "end": v(145.62, 32.5) * mm});
            skLineSegment(sketch, "E91.2.1.99", {"start": v(145.62, 77.5) * mm, "end": v(147.62, 77.5) * mm});
            skLineSegment(sketch, "E91.2.1.100", {"start": v(145.62, 72.5) * mm, "end": v(147.62, 72.5) * mm});
            skArc(sketch, "E91.2.1.101", {"start": v(148.62, 36.5) * mm, "mid": v(148.33, 37.2) * mm, "end": v(147.62, 37.5) * mm});
            skLineSegment(sketch, "E91.2.1.102", {"start": v(145.62, 77.5) * mm, "end": v(145.62, 72.5) * mm});
            skArc(sketch, "E91.2.1.103", {"start": v(147.62, 32.5) * mm, "mid": v(148.33, 32.8) * mm, "end": v(148.62, 33.5) * mm});
            skLineSegment(sketch, "E91.2.1.104", {"start": v(148.62, 76.5) * mm, "end": v(148.62, 73.5) * mm});
            skArc(sketch, "E91.2.1.105", {"start": v(148.62, 56.5) * mm, "mid": v(148.33, 57.2) * mm, "end": v(147.62, 57.5) * mm});
            skLineSegment(sketch, "E91.2.1.106", {"start": v(145.62, 57.5) * mm, "end": v(147.62, 57.5) * mm});
            skArc(sketch, "E91.2.1.107", {"start": v(138.25, 59.5) * mm, "mid": v(138.84, 58.09) * mm, "end": v(140.25, 57.5) * mm});
            skArc(sketch, "E91.2.1.108", {"start": v(147.62, 72.5) * mm, "mid": v(148.33, 72.8) * mm, "end": v(148.62, 73.5) * mm});
            skArc(sketch, "E91.2.1.109", {"start": v(148.62, 76.5) * mm, "mid": v(148.33, 77.2) * mm, "end": v(147.62, 77.5) * mm});
            skLineSegment(sketch, "E91.2.1.110", {"start": v(145.62, 37.5) * mm, "end": v(147.62, 37.5) * mm});
            skLineSegment(sketch, "E91.2.1.111", {"start": v(145.62, 32.5) * mm, "end": v(147.62, 32.5) * mm});
            skLineSegment(sketch, "E91.2.1.112", {"start": v(148.62, 36.5) * mm, "end": v(148.62, 33.5) * mm});
            skLineSegment(sketch, "E91.2.1.113", {"start": v(145.62, 77.5) * mm, "end": v(145.62, 72.5) * mm});
            skArc(sketch, "E91.2.1.114", {"start": v(147.62, 52.5) * mm, "mid": v(148.33, 52.8) * mm, "end": v(148.62, 53.5) * mm});
            skLineSegment(sketch, "E91.2.1.115", {"start": v(145.62, 52.5) * mm, "end": v(147.62, 52.5) * mm});
            skLineSegment(sketch, "E91.2.1.116", {"start": v(148.62, 56.5) * mm, "end": v(148.62, 53.5) * mm});
            skLineSegment(sketch, "E91.2.1.117", {"start": v(145.62, 37.5) * mm, "end": v(145.62, 32.5) * mm});
            skLineSegment(sketch, "E91.2.1.118", {"start": v(145.62, 57.5) * mm, "end": v(145.62, 52.5) * mm});
            skLineSegment(sketch, "E91.2.1.119", {"start": v(145.62, 57.5) * mm, "end": v(145.62, 52.5) * mm});
            skLineSegment(sketch, "E91.direction1", {"start": v(-25.63, -22.5) * mm, "end": v(34.37, -22.5) * mm, "construction": true});
            skLineSegment(sketch, "E91.direction2", {"start": v(-25.63, -22.5) * mm, "end": v(-25.63, 32.5) * mm, "construction": true});
            skSolve(sketch);
        }
        {
            var Q0;
            Q0=qSketchRegion(id+"F0",true);
            extrude(context, id + "F1", {"entities" : qUnion([Q0]), "depth" : .4 * mm});
        }
        {
            var Q0;
            Q0=qCreatedBy(makeId("Top.planeOp"),FACE);
            var sketch = newSketch(context, id + "F2", { "sketchPlane" : qUnion([Q0])});
            skLineSegment(sketch, "E92.bottom", {"start": v(165, 88) * mm, "end": v(-35, 88) * mm});
            skLineSegment(sketch, "E92.top", {"start": v(165, -32) * mm, "end": v(-35, -32) * mm});
            skLineSegment(sketch, "E92.left", {"start": v(165, 88) * mm, "end": v(165, -32) * mm});
            skLineSegment(sketch, "E92.right", {"start": v(-35, 88) * mm, "end": v(-35, -32) * mm});
            skSolve(sketch);
        }
        {
            var Q0;
            Q0=makeQuery(id+"F2.imprint","IMPRINT",FACE,{"disambiguationData":[TD([[makeQuery(id+"F2.imprint","IMPRINT",EDGE,{"derivedFrom":sQuery(id+"F2.wireOp",EDGE,"E92.bottom")}),1.0]])]});
            extrude(context, id + "F3", {"entities" : qUnion([Q0]), "oppositeDirection" : true, "depth" : 2 * mm});
        }
        {
            var Q0;
            Q0=makeQuery(id+"F3.opExtrude","SWEPT_BODY",BODY,{"disambiguationData":[OSD([sQuery(id+"F2.wireOp",EDGE,"E92.bottom"),sQuery(id+"F2.wireOp",EDGE,"E92.top"),sQuery(id+"F2.wireOp",EDGE,"E92.left"),sQuery(id+"F2.wireOp",EDGE,"E92.right")])]});
            transform(context, id + "F4", {"entities" : qUnion([Q0]), "transformType" : TransformType.TRANSLATION_3D, "dx" : 0 * mm, "dy" : 0 * mm, "dz" : .4 * mm, "makeCopy" : false});
        }
        {
            var Q0;
            Q0=makeQuery(id+"F1.opExtrude","SWEPT_BODY",BODY,{"disambiguationData":[OSD([sQuery(id+"F0.wireOp",EDGE,"E0.bottom"),sQuery(id+"F0.wireOp",EDGE,"E0.top"),sQuery(id+"F0.wireOp",EDGE,"E0.left"),sQuery(id+"F0.wireOp",EDGE,"E0.right"),sQuery(id+"F0.wireOp",EDGE,"E1.filletArc"),sQuery(id+"F0.wireOp",EDGE,"E2.filletArc"),sQuery(id+"F0.wireOp",EDGE,"E3.filletArc"),sQuery(id+"F0.wireOp",EDGE,"E4.filletArc"),sQuery(id+"F0.wireOp",EDGE,"E5.MirrorCS"),sQuery(id+"F0.wireOp",EDGE,"E6.MirrorCS"),sQuery(id+"F0.wireOp",EDGE,"E7.MirrorCS"),sQuery(id+"F0.wireOp",EDGE,"E8.MirrorCS"),sQuery(id+"F0.wireOp",EDGE,"E9.MirrorCS"),sQuery(id+"F0.wireOp",EDGE,"E10.MirrorCS"),sQuery(id+"F0.wireOp",EDGE,"E15.MirrorCS"),sQuery(id+"F0.wireOp",EDGE,"E16.MirrorCS"),sQuery(id+"F0.wireOp",EDGE,"E17.MirrorCS"),sQuery(id+"F0.wireOp",EDGE,"E18.MirrorCS"),sQuery(id+"F0.wireOp",EDGE,"E19.MirrorCS"),sQuery(id+"F0.wireOp",EDGE,"E20.MirrorCS"),sQuery(id+"F0.wireOp",EDGE,"E21.MirrorCS"),sQuery(id+"F0.wireOp",EDGE,"E22.MirrorCS"),sQuery(id+"F0.wireOp",EDGE,"E23.MirrorCS"),sQuery(id+"F0.wireOp",EDGE,"E24.MirrorCS"),sQuery(id+"F0.wireOp",EDGE,"E26.MirrorCS"),sQuery(id+"F0.wireOp",EDGE,"E27.MirrorCS"),sQuery(id+"F0.wireOp",EDGE,"E29.MirrorCS"),sQuery(id+"F0.wireOp",EDGE,"E30.MirrorCS"),sQuery(id+"F0.wireOp",EDGE,"E31.MirrorCS"),sQuery(id+"F0.wireOp",EDGE,"E33.MirrorCS"),sQuery(id+"F0.wireOp",EDGE,"E34.MirrorCS"),sQuery(id+"F0.wireOp",EDGE,"E40.MirrorCS"),sQuery(id+"F0.wireOp",EDGE,"E42.MirrorCS"),sQuery(id+"F0.wireOp",EDGE,"E43.MirrorCS"),sQuery(id+"F0.wireOp",EDGE,"E44.MirrorCS"),sQuery(id+"F0.wireOp",EDGE,"E45.MirrorCS"),sQuery(id+"F0.wireOp",EDGE,"E46.MirrorCS"),sQuery(id+"F0.wireOp",EDGE,"E47.MirrorCS"),sQuery(id+"F0.wireOp",EDGE,"E50.MirrorCS"),sQuery(id+"F0.wireOp",EDGE,"E52.MirrorCS"),sQuery(id+"F0.wireOp",EDGE,"E53.MirrorCS"),sQuery(id+"F0.wireOp",EDGE,"E55.MirrorCS"),sQuery(id+"F0.wireOp",EDGE,"E56.bottom"),sQuery(id+"F0.wireOp",EDGE,"E56.top"),sQuery(id+"F0.wireOp",EDGE,"E57.MirrorCS"),sQuery(id+"F0.wireOp",EDGE,"E58.MirrorCS"),sQuery(id+"F0.wireOp",EDGE,"E59.MirrorCS"),sQuery(id+"F0.wireOp",EDGE,"E60.MirrorCS"),sQuery(id+"F0.wireOp",EDGE,"E62.MirrorCS"),sQuery(id+"F0.wireOp",EDGE,"E63.MirrorCS"),sQuery(id+"F0.wireOp",EDGE,"E66.MirrorCS"),sQuery(id+"F0.wireOp",EDGE,"E68.MirrorCS"),sQuery(id+"F0.wireOp",EDGE,"E69.MirrorCS"),sQuery(id+"F0.wireOp",EDGE,"E70.MirrorCS"),sQuery(id+"F0.wireOp",EDGE,"E71.MirrorCS"),sQuery(id+"F0.wireOp",EDGE,"E74.trimOffspring"),sQuery(id+"F0.wireOp",EDGE,"E75.trimOffspring"),sQuery(id+"F0.wireOp",EDGE,"E76.bottom"),sQuery(id+"F0.wireOp",EDGE,"E76.top"),sQuery(id+"F0.wireOp",EDGE,"E76.right"),sQuery(id+"F0.wireOp",EDGE,"E77.bottom"),sQuery(id+"F0.wireOp",EDGE,"E77.top"),sQuery(id+"F0.wireOp",EDGE,"E77.right"),sQuery(id+"F0.wireOp",EDGE,"E78.bottom"),sQuery(id+"F0.wireOp",EDGE,"E78.top"),sQuery(id+"F0.wireOp",EDGE,"E78.right"),sQuery(id+"F0.wireOp",EDGE,"E79.filletArc"),sQuery(id+"F0.wireOp",EDGE,"E80.filletArc"),sQuery(id+"F0.wireOp",EDGE,"E81.filletArc"),sQuery(id+"F0.wireOp",EDGE,"E82.filletArc"),sQuery(id+"F0.wireOp",EDGE,"E83.filletArc"),sQuery(id+"F0.wireOp",EDGE,"E84.filletArc"),sQuery(id+"F0.wireOp",EDGE,"E85.filletArc"),sQuery(id+"F0.wireOp",EDGE,"E86.filletArc"),sQuery(id+"F0.wireOp",EDGE,"E87.filletArc"),sQuery(id+"F0.wireOp",EDGE,"E88.filletArc"),sQuery(id+"F0.wireOp",EDGE,"E89.filletArc"),sQuery(id+"F0.wireOp",EDGE,"E90.filletArc")])]});
            var Q1;
            Q1=makeQuery(id+"F1.opExtrude","SWEPT_BODY",BODY,{"disambiguationData":[OSD([sQuery(id+"F0.wireOp",EDGE,"E91.2.1.3"),sQuery(id+"F0.wireOp",EDGE,"E91.2.1.4"),sQuery(id+"F0.wireOp",EDGE,"E91.2.1.5"),sQuery(id+"F0.wireOp",EDGE,"E91.2.1.10"),sQuery(id+"F0.wireOp",EDGE,"E91.2.1.11"),sQuery(id+"F0.wireOp",EDGE,"E91.2.1.12"),sQuery(id+"F0.wireOp",EDGE,"E91.2.1.17"),sQuery(id+"F0.wireOp",EDGE,"E91.2.1.18"),sQuery(id+"F0.wireOp",EDGE,"E91.2.1.19"),sQuery(id+"F0.wireOp",EDGE,"E91.2.1.20"),sQuery(id+"F0.wireOp",EDGE,"E91.2.1.21"),sQuery(id+"F0.wireOp",EDGE,"E91.2.1.22"),sQuery(id+"F0.wireOp",EDGE,"E91.2.1.23"),sQuery(id+"F0.wireOp",EDGE,"E91.2.1.32"),sQuery(id+"F0.wireOp",EDGE,"E91.2.1.42"),sQuery(id+"F0.wireOp",EDGE,"E91.2.1.48"),sQuery(id+"F0.wireOp",EDGE,"E91.2.1.49"),sQuery(id+"F0.wireOp",EDGE,"E91.2.1.50"),sQuery(id+"F0.wireOp",EDGE,"E91.2.1.51"),sQuery(id+"F0.wireOp",EDGE,"E91.2.1.52"),sQuery(id+"F0.wireOp",EDGE,"E91.2.1.54"),sQuery(id+"F0.wireOp",EDGE,"E91.2.1.55"),sQuery(id+"F0.wireOp",EDGE,"E91.2.1.58"),sQuery(id+"F0.wireOp",EDGE,"E91.2.1.59"),sQuery(id+"F0.wireOp",EDGE,"E91.2.1.60"),sQuery(id+"F0.wireOp",EDGE,"E91.2.1.61"),sQuery(id+"F0.wireOp",EDGE,"E91.2.1.62"),sQuery(id+"F0.wireOp",EDGE,"E91.2.1.63"),sQuery(id+"F0.wireOp",EDGE,"E91.2.1.64"),sQuery(id+"F0.wireOp",EDGE,"E91.2.1.65"),sQuery(id+"F0.wireOp",EDGE,"E91.2.1.66"),sQuery(id+"F0.wireOp",EDGE,"E91.2.1.67"),sQuery(id+"F0.wireOp",EDGE,"E91.2.1.68"),sQuery(id+"F0.wireOp",EDGE,"E91.2.1.69"),sQuery(id+"F0.wireOp",EDGE,"E91.2.1.70"),sQuery(id+"F0.wireOp",EDGE,"E91.2.1.71"),sQuery(id+"F0.wireOp",EDGE,"E91.2.1.72"),sQuery(id+"F0.wireOp",EDGE,"E91.2.1.73"),sQuery(id+"F0.wireOp",EDGE,"E91.2.1.74"),sQuery(id+"F0.wireOp",EDGE,"E91.2.1.75"),sQuery(id+"F0.wireOp",EDGE,"E91.2.1.76"),sQuery(id+"F0.wireOp",EDGE,"E91.2.1.77"),sQuery(id+"F0.wireOp",EDGE,"E91.2.1.78"),sQuery(id+"F0.wireOp",EDGE,"E91.2.1.79"),sQuery(id+"F0.wireOp",EDGE,"E91.2.1.80"),sQuery(id+"F0.wireOp",EDGE,"E91.2.1.81"),sQuery(id+"F0.wireOp",EDGE,"E91.2.1.82"),sQuery(id+"F0.wireOp",EDGE,"E91.2.1.83"),sQuery(id+"F0.wireOp",EDGE,"E91.2.1.84"),sQuery(id+"F0.wireOp",EDGE,"E91.2.1.85"),sQuery(id+"F0.wireOp",EDGE,"E91.2.1.86"),sQuery(id+"F0.wireOp",EDGE,"E91.2.1.87"),sQuery(id+"F0.wireOp",EDGE,"E91.2.1.88"),sQuery(id+"F0.wireOp",EDGE,"E91.2.1.89"),sQuery(id+"F0.wireOp",EDGE,"E91.2.1.90"),sQuery(id+"F0.wireOp",EDGE,"E91.2.1.91"),sQuery(id+"F0.wireOp",EDGE,"E91.2.1.92"),sQuery(id+"F0.wireOp",EDGE,"E91.2.1.93"),sQuery(id+"F0.wireOp",EDGE,"E91.2.1.94"),sQuery(id+"F0.wireOp",EDGE,"E91.2.1.95"),sQuery(id+"F0.wireOp",EDGE,"E91.2.1.96"),sQuery(id+"F0.wireOp",EDGE,"E91.2.1.97"),sQuery(id+"F0.wireOp",EDGE,"E91.2.1.99"),sQuery(id+"F0.wireOp",EDGE,"E91.2.1.100"),sQuery(id+"F0.wireOp",EDGE,"E91.2.1.101"),sQuery(id+"F0.wireOp",EDGE,"E91.2.1.103"),sQuery(id+"F0.wireOp",EDGE,"E91.2.1.104"),sQuery(id+"F0.wireOp",EDGE,"E91.2.1.105"),sQuery(id+"F0.wireOp",EDGE,"E91.2.1.106"),sQuery(id+"F0.wireOp",EDGE,"E91.2.1.107"),sQuery(id+"F0.wireOp",EDGE,"E91.2.1.108"),sQuery(id+"F0.wireOp",EDGE,"E91.2.1.109"),sQuery(id+"F0.wireOp",EDGE,"E91.2.1.110"),sQuery(id+"F0.wireOp",EDGE,"E91.2.1.111"),sQuery(id+"F0.wireOp",EDGE,"E91.2.1.112"),sQuery(id+"F0.wireOp",EDGE,"E91.2.1.114"),sQuery(id+"F0.wireOp",EDGE,"E91.2.1.115"),sQuery(id+"F0.wireOp",EDGE,"E91.2.1.116")])]});
            var Q2;
            Q2=makeQuery(id+"F1.opExtrude","SWEPT_BODY",BODY,{"disambiguationData":[OSD([sQuery(id+"F0.wireOp",EDGE,"E91.2.0.3"),sQuery(id+"F0.wireOp",EDGE,"E91.2.0.4"),sQuery(id+"F0.wireOp",EDGE,"E91.2.0.5"),sQuery(id+"F0.wireOp",EDGE,"E91.2.0.10"),sQuery(id+"F0.wireOp",EDGE,"E91.2.0.11"),sQuery(id+"F0.wireOp",EDGE,"E91.2.0.12"),sQuery(id+"F0.wireOp",EDGE,"E91.2.0.17"),sQuery(id+"F0.wireOp",EDGE,"E91.2.0.18"),sQuery(id+"F0.wireOp",EDGE,"E91.2.0.19"),sQuery(id+"F0.wireOp",EDGE,"E91.2.0.20"),sQuery(id+"F0.wireOp",EDGE,"E91.2.0.21"),sQuery(id+"F0.wireOp",EDGE,"E91.2.0.22"),sQuery(id+"F0.wireOp",EDGE,"E91.2.0.23"),sQuery(id+"F0.wireOp",EDGE,"E91.2.0.32"),sQuery(id+"F0.wireOp",EDGE,"E91.2.0.42"),sQuery(id+"F0.wireOp",EDGE,"E91.2.0.48"),sQuery(id+"F0.wireOp",EDGE,"E91.2.0.49"),sQuery(id+"F0.wireOp",EDGE,"E91.2.0.50"),sQuery(id+"F0.wireOp",EDGE,"E91.2.0.51"),sQuery(id+"F0.wireOp",EDGE,"E91.2.0.52"),sQuery(id+"F0.wireOp",EDGE,"E91.2.0.54"),sQuery(id+"F0.wireOp",EDGE,"E91.2.0.55"),sQuery(id+"F0.wireOp",EDGE,"E91.2.0.58"),sQuery(id+"F0.wireOp",EDGE,"E91.2.0.59"),sQuery(id+"F0.wireOp",EDGE,"E91.2.0.60"),sQuery(id+"F0.wireOp",EDGE,"E91.2.0.61"),sQuery(id+"F0.wireOp",EDGE,"E91.2.0.62"),sQuery(id+"F0.wireOp",EDGE,"E91.2.0.63"),sQuery(id+"F0.wireOp",EDGE,"E91.2.0.64"),sQuery(id+"F0.wireOp",EDGE,"E91.2.0.65"),sQuery(id+"F0.wireOp",EDGE,"E91.2.0.66"),sQuery(id+"F0.wireOp",EDGE,"E91.2.0.67"),sQuery(id+"F0.wireOp",EDGE,"E91.2.0.68"),sQuery(id+"F0.wireOp",EDGE,"E91.2.0.69"),sQuery(id+"F0.wireOp",EDGE,"E91.2.0.70"),sQuery(id+"F0.wireOp",EDGE,"E91.2.0.71"),sQuery(id+"F0.wireOp",EDGE,"E91.2.0.72"),sQuery(id+"F0.wireOp",EDGE,"E91.2.0.73"),sQuery(id+"F0.wireOp",EDGE,"E91.2.0.74"),sQuery(id+"F0.wireOp",EDGE,"E91.2.0.75"),sQuery(id+"F0.wireOp",EDGE,"E91.2.0.76"),sQuery(id+"F0.wireOp",EDGE,"E91.2.0.77"),sQuery(id+"F0.wireOp",EDGE,"E91.2.0.78"),sQuery(id+"F0.wireOp",EDGE,"E91.2.0.79"),sQuery(id+"F0.wireOp",EDGE,"E91.2.0.80"),sQuery(id+"F0.wireOp",EDGE,"E91.2.0.81"),sQuery(id+"F0.wireOp",EDGE,"E91.2.0.82"),sQuery(id+"F0.wireOp",EDGE,"E91.2.0.83"),sQuery(id+"F0.wireOp",EDGE,"E91.2.0.84"),sQuery(id+"F0.wireOp",EDGE,"E91.2.0.85"),sQuery(id+"F0.wireOp",EDGE,"E91.2.0.86"),sQuery(id+"F0.wireOp",EDGE,"E91.2.0.87"),sQuery(id+"F0.wireOp",EDGE,"E91.2.0.88"),sQuery(id+"F0.wireOp",EDGE,"E91.2.0.89"),sQuery(id+"F0.wireOp",EDGE,"E91.2.0.90"),sQuery(id+"F0.wireOp",EDGE,"E91.2.0.91"),sQuery(id+"F0.wireOp",EDGE,"E91.2.0.92"),sQuery(id+"F0.wireOp",EDGE,"E91.2.0.93"),sQuery(id+"F0.wireOp",EDGE,"E91.2.0.94"),sQuery(id+"F0.wireOp",EDGE,"E91.2.0.95"),sQuery(id+"F0.wireOp",EDGE,"E91.2.0.96"),sQuery(id+"F0.wireOp",EDGE,"E91.2.0.97"),sQuery(id+"F0.wireOp",EDGE,"E91.2.0.99"),sQuery(id+"F0.wireOp",EDGE,"E91.2.0.100"),sQuery(id+"F0.wireOp",EDGE,"E91.2.0.101"),sQuery(id+"F0.wireOp",EDGE,"E91.2.0.103"),sQuery(id+"F0.wireOp",EDGE,"E91.2.0.104"),sQuery(id+"F0.wireOp",EDGE,"E91.2.0.105"),sQuery(id+"F0.wireOp",EDGE,"E91.2.0.106"),sQuery(id+"F0.wireOp",EDGE,"E91.2.0.107"),sQuery(id+"F0.wireOp",EDGE,"E91.2.0.108"),sQuery(id+"F0.wireOp",EDGE,"E91.2.0.109"),sQuery(id+"F0.wireOp",EDGE,"E91.2.0.110"),sQuery(id+"F0.wireOp",EDGE,"E91.2.0.111"),sQuery(id+"F0.wireOp",EDGE,"E91.2.0.112"),sQuery(id+"F0.wireOp",EDGE,"E91.2.0.114"),sQuery(id+"F0.wireOp",EDGE,"E91.2.0.115"),sQuery(id+"F0.wireOp",EDGE,"E91.2.0.116")])]});
            var Q3;
            Q3=makeQuery(id+"F1.opExtrude","SWEPT_BODY",BODY,{"disambiguationData":[OSD([sQuery(id+"F0.wireOp",EDGE,"E91.1.1.3"),sQuery(id+"F0.wireOp",EDGE,"E91.1.1.4"),sQuery(id+"F0.wireOp",EDGE,"E91.1.1.5"),sQuery(id+"F0.wireOp",EDGE,"E91.1.1.10"),sQuery(id+"F0.wireOp",EDGE,"E91.1.1.11"),sQuery(id+"F0.wireOp",EDGE,"E91.1.1.12"),sQuery(id+"F0.wireOp",EDGE,"E91.1.1.17"),sQuery(id+"F0.wireOp",EDGE,"E91.1.1.18"),sQuery(id+"F0.wireOp",EDGE,"E91.1.1.19"),sQuery(id+"F0.wireOp",EDGE,"E91.1.1.20"),sQuery(id+"F0.wireOp",EDGE,"E91.1.1.21"),sQuery(id+"F0.wireOp",EDGE,"E91.1.1.22"),sQuery(id+"F0.wireOp",EDGE,"E91.1.1.23"),sQuery(id+"F0.wireOp",EDGE,"E91.1.1.32"),sQuery(id+"F0.wireOp",EDGE,"E91.1.1.42"),sQuery(id+"F0.wireOp",EDGE,"E91.1.1.48"),sQuery(id+"F0.wireOp",EDGE,"E91.1.1.49"),sQuery(id+"F0.wireOp",EDGE,"E91.1.1.50"),sQuery(id+"F0.wireOp",EDGE,"E91.1.1.51"),sQuery(id+"F0.wireOp",EDGE,"E91.1.1.52"),sQuery(id+"F0.wireOp",EDGE,"E91.1.1.54"),sQuery(id+"F0.wireOp",EDGE,"E91.1.1.55"),sQuery(id+"F0.wireOp",EDGE,"E91.1.1.58"),sQuery(id+"F0.wireOp",EDGE,"E91.1.1.59"),sQuery(id+"F0.wireOp",EDGE,"E91.1.1.60"),sQuery(id+"F0.wireOp",EDGE,"E91.1.1.61"),sQuery(id+"F0.wireOp",EDGE,"E91.1.1.62"),sQuery(id+"F0.wireOp",EDGE,"E91.1.1.63"),sQuery(id+"F0.wireOp",EDGE,"E91.1.1.64"),sQuery(id+"F0.wireOp",EDGE,"E91.1.1.65"),sQuery(id+"F0.wireOp",EDGE,"E91.1.1.66"),sQuery(id+"F0.wireOp",EDGE,"E91.1.1.67"),sQuery(id+"F0.wireOp",EDGE,"E91.1.1.68"),sQuery(id+"F0.wireOp",EDGE,"E91.1.1.69"),sQuery(id+"F0.wireOp",EDGE,"E91.1.1.70"),sQuery(id+"F0.wireOp",EDGE,"E91.1.1.71"),sQuery(id+"F0.wireOp",EDGE,"E91.1.1.72"),sQuery(id+"F0.wireOp",EDGE,"E91.1.1.73"),sQuery(id+"F0.wireOp",EDGE,"E91.1.1.74"),sQuery(id+"F0.wireOp",EDGE,"E91.1.1.75"),sQuery(id+"F0.wireOp",EDGE,"E91.1.1.76"),sQuery(id+"F0.wireOp",EDGE,"E91.1.1.77"),sQuery(id+"F0.wireOp",EDGE,"E91.1.1.78"),sQuery(id+"F0.wireOp",EDGE,"E91.1.1.79"),sQuery(id+"F0.wireOp",EDGE,"E91.1.1.80"),sQuery(id+"F0.wireOp",EDGE,"E91.1.1.81"),sQuery(id+"F0.wireOp",EDGE,"E91.1.1.82"),sQuery(id+"F0.wireOp",EDGE,"E91.1.1.83"),sQuery(id+"F0.wireOp",EDGE,"E91.1.1.84"),sQuery(id+"F0.wireOp",EDGE,"E91.1.1.85"),sQuery(id+"F0.wireOp",EDGE,"E91.1.1.86"),sQuery(id+"F0.wireOp",EDGE,"E91.1.1.87"),sQuery(id+"F0.wireOp",EDGE,"E91.1.1.88"),sQuery(id+"F0.wireOp",EDGE,"E91.1.1.89"),sQuery(id+"F0.wireOp",EDGE,"E91.1.1.90"),sQuery(id+"F0.wireOp",EDGE,"E91.1.1.91"),sQuery(id+"F0.wireOp",EDGE,"E91.1.1.92"),sQuery(id+"F0.wireOp",EDGE,"E91.1.1.93"),sQuery(id+"F0.wireOp",EDGE,"E91.1.1.94"),sQuery(id+"F0.wireOp",EDGE,"E91.1.1.95"),sQuery(id+"F0.wireOp",EDGE,"E91.1.1.96"),sQuery(id+"F0.wireOp",EDGE,"E91.1.1.97"),sQuery(id+"F0.wireOp",EDGE,"E91.1.1.99"),sQuery(id+"F0.wireOp",EDGE,"E91.1.1.100"),sQuery(id+"F0.wireOp",EDGE,"E91.1.1.101"),sQuery(id+"F0.wireOp",EDGE,"E91.1.1.103"),sQuery(id+"F0.wireOp",EDGE,"E91.1.1.104"),sQuery(id+"F0.wireOp",EDGE,"E91.1.1.105"),sQuery(id+"F0.wireOp",EDGE,"E91.1.1.106"),sQuery(id+"F0.wireOp",EDGE,"E91.1.1.107"),sQuery(id+"F0.wireOp",EDGE,"E91.1.1.108"),sQuery(id+"F0.wireOp",EDGE,"E91.1.1.109"),sQuery(id+"F0.wireOp",EDGE,"E91.1.1.110"),sQuery(id+"F0.wireOp",EDGE,"E91.1.1.111"),sQuery(id+"F0.wireOp",EDGE,"E91.1.1.112"),sQuery(id+"F0.wireOp",EDGE,"E91.1.1.114"),sQuery(id+"F0.wireOp",EDGE,"E91.1.1.115"),sQuery(id+"F0.wireOp",EDGE,"E91.1.1.116")])]});
            var Q4;
            Q4=makeQuery(id+"F1.opExtrude","SWEPT_BODY",BODY,{"disambiguationData":[OSD([sQuery(id+"F0.wireOp",EDGE,"E91.1.0.3"),sQuery(id+"F0.wireOp",EDGE,"E91.1.0.4"),sQuery(id+"F0.wireOp",EDGE,"E91.1.0.5"),sQuery(id+"F0.wireOp",EDGE,"E91.1.0.10"),sQuery(id+"F0.wireOp",EDGE,"E91.1.0.11"),sQuery(id+"F0.wireOp",EDGE,"E91.1.0.12"),sQuery(id+"F0.wireOp",EDGE,"E91.1.0.17"),sQuery(id+"F0.wireOp",EDGE,"E91.1.0.18"),sQuery(id+"F0.wireOp",EDGE,"E91.1.0.19"),sQuery(id+"F0.wireOp",EDGE,"E91.1.0.20"),sQuery(id+"F0.wireOp",EDGE,"E91.1.0.21"),sQuery(id+"F0.wireOp",EDGE,"E91.1.0.22"),sQuery(id+"F0.wireOp",EDGE,"E91.1.0.23"),sQuery(id+"F0.wireOp",EDGE,"E91.1.0.32"),sQuery(id+"F0.wireOp",EDGE,"E91.1.0.42"),sQuery(id+"F0.wireOp",EDGE,"E91.1.0.48"),sQuery(id+"F0.wireOp",EDGE,"E91.1.0.49"),sQuery(id+"F0.wireOp",EDGE,"E91.1.0.50"),sQuery(id+"F0.wireOp",EDGE,"E91.1.0.51"),sQuery(id+"F0.wireOp",EDGE,"E91.1.0.52"),sQuery(id+"F0.wireOp",EDGE,"E91.1.0.54"),sQuery(id+"F0.wireOp",EDGE,"E91.1.0.55"),sQuery(id+"F0.wireOp",EDGE,"E91.1.0.58"),sQuery(id+"F0.wireOp",EDGE,"E91.1.0.59"),sQuery(id+"F0.wireOp",EDGE,"E91.1.0.60"),sQuery(id+"F0.wireOp",EDGE,"E91.1.0.61"),sQuery(id+"F0.wireOp",EDGE,"E91.1.0.62"),sQuery(id+"F0.wireOp",EDGE,"E91.1.0.63"),sQuery(id+"F0.wireOp",EDGE,"E91.1.0.64"),sQuery(id+"F0.wireOp",EDGE,"E91.1.0.65"),sQuery(id+"F0.wireOp",EDGE,"E91.1.0.66"),sQuery(id+"F0.wireOp",EDGE,"E91.1.0.67"),sQuery(id+"F0.wireOp",EDGE,"E91.1.0.68"),sQuery(id+"F0.wireOp",EDGE,"E91.1.0.69"),sQuery(id+"F0.wireOp",EDGE,"E91.1.0.70"),sQuery(id+"F0.wireOp",EDGE,"E91.1.0.71"),sQuery(id+"F0.wireOp",EDGE,"E91.1.0.72"),sQuery(id+"F0.wireOp",EDGE,"E91.1.0.73"),sQuery(id+"F0.wireOp",EDGE,"E91.1.0.74"),sQuery(id+"F0.wireOp",EDGE,"E91.1.0.75"),sQuery(id+"F0.wireOp",EDGE,"E91.1.0.76"),sQuery(id+"F0.wireOp",EDGE,"E91.1.0.77"),sQuery(id+"F0.wireOp",EDGE,"E91.1.0.78"),sQuery(id+"F0.wireOp",EDGE,"E91.1.0.79"),sQuery(id+"F0.wireOp",EDGE,"E91.1.0.80"),sQuery(id+"F0.wireOp",EDGE,"E91.1.0.81"),sQuery(id+"F0.wireOp",EDGE,"E91.1.0.82"),sQuery(id+"F0.wireOp",EDGE,"E91.1.0.83"),sQuery(id+"F0.wireOp",EDGE,"E91.1.0.84"),sQuery(id+"F0.wireOp",EDGE,"E91.1.0.85"),sQuery(id+"F0.wireOp",EDGE,"E91.1.0.86"),sQuery(id+"F0.wireOp",EDGE,"E91.1.0.87"),sQuery(id+"F0.wireOp",EDGE,"E91.1.0.88"),sQuery(id+"F0.wireOp",EDGE,"E91.1.0.89"),sQuery(id+"F0.wireOp",EDGE,"E91.1.0.90"),sQuery(id+"F0.wireOp",EDGE,"E91.1.0.91"),sQuery(id+"F0.wireOp",EDGE,"E91.1.0.92"),sQuery(id+"F0.wireOp",EDGE,"E91.1.0.93"),sQuery(id+"F0.wireOp",EDGE,"E91.1.0.94"),sQuery(id+"F0.wireOp",EDGE,"E91.1.0.95"),sQuery(id+"F0.wireOp",EDGE,"E91.1.0.96"),sQuery(id+"F0.wireOp",EDGE,"E91.1.0.97"),sQuery(id+"F0.wireOp",EDGE,"E91.1.0.99"),sQuery(id+"F0.wireOp",EDGE,"E91.1.0.100"),sQuery(id+"F0.wireOp",EDGE,"E91.1.0.101"),sQuery(id+"F0.wireOp",EDGE,"E91.1.0.103"),sQuery(id+"F0.wireOp",EDGE,"E91.1.0.104"),sQuery(id+"F0.wireOp",EDGE,"E91.1.0.105"),sQuery(id+"F0.wireOp",EDGE,"E91.1.0.106"),sQuery(id+"F0.wireOp",EDGE,"E91.1.0.107"),sQuery(id+"F0.wireOp",EDGE,"E91.1.0.108"),sQuery(id+"F0.wireOp",EDGE,"E91.1.0.109"),sQuery(id+"F0.wireOp",EDGE,"E91.1.0.110"),sQuery(id+"F0.wireOp",EDGE,"E91.1.0.111"),sQuery(id+"F0.wireOp",EDGE,"E91.1.0.112"),sQuery(id+"F0.wireOp",EDGE,"E91.1.0.114"),sQuery(id+"F0.wireOp",EDGE,"E91.1.0.115"),sQuery(id+"F0.wireOp",EDGE,"E91.1.0.116")])]});
            var Q5;
            Q5=makeQuery(id+"F1.opExtrude","SWEPT_BODY",BODY,{"disambiguationData":[OSD([sQuery(id+"F0.wireOp",EDGE,"E91.0.1.3"),sQuery(id+"F0.wireOp",EDGE,"E91.0.1.4"),sQuery(id+"F0.wireOp",EDGE,"E91.0.1.5"),sQuery(id+"F0.wireOp",EDGE,"E91.0.1.10"),sQuery(id+"F0.wireOp",EDGE,"E91.0.1.11"),sQuery(id+"F0.wireOp",EDGE,"E91.0.1.12"),sQuery(id+"F0.wireOp",EDGE,"E91.0.1.17"),sQuery(id+"F0.wireOp",EDGE,"E91.0.1.18"),sQuery(id+"F0.wireOp",EDGE,"E91.0.1.19"),sQuery(id+"F0.wireOp",EDGE,"E91.0.1.20"),sQuery(id+"F0.wireOp",EDGE,"E91.0.1.21"),sQuery(id+"F0.wireOp",EDGE,"E91.0.1.22"),sQuery(id+"F0.wireOp",EDGE,"E91.0.1.23"),sQuery(id+"F0.wireOp",EDGE,"E91.0.1.32"),sQuery(id+"F0.wireOp",EDGE,"E91.0.1.42"),sQuery(id+"F0.wireOp",EDGE,"E91.0.1.48"),sQuery(id+"F0.wireOp",EDGE,"E91.0.1.49"),sQuery(id+"F0.wireOp",EDGE,"E91.0.1.50"),sQuery(id+"F0.wireOp",EDGE,"E91.0.1.51"),sQuery(id+"F0.wireOp",EDGE,"E91.0.1.52"),sQuery(id+"F0.wireOp",EDGE,"E91.0.1.54"),sQuery(id+"F0.wireOp",EDGE,"E91.0.1.55"),sQuery(id+"F0.wireOp",EDGE,"E91.0.1.58"),sQuery(id+"F0.wireOp",EDGE,"E91.0.1.59"),sQuery(id+"F0.wireOp",EDGE,"E91.0.1.60"),sQuery(id+"F0.wireOp",EDGE,"E91.0.1.61"),sQuery(id+"F0.wireOp",EDGE,"E91.0.1.62"),sQuery(id+"F0.wireOp",EDGE,"E91.0.1.63"),sQuery(id+"F0.wireOp",EDGE,"E91.0.1.64"),sQuery(id+"F0.wireOp",EDGE,"E91.0.1.65"),sQuery(id+"F0.wireOp",EDGE,"E91.0.1.66"),sQuery(id+"F0.wireOp",EDGE,"E91.0.1.67"),sQuery(id+"F0.wireOp",EDGE,"E91.0.1.68"),sQuery(id+"F0.wireOp",EDGE,"E91.0.1.69"),sQuery(id+"F0.wireOp",EDGE,"E91.0.1.70"),sQuery(id+"F0.wireOp",EDGE,"E91.0.1.71"),sQuery(id+"F0.wireOp",EDGE,"E91.0.1.72"),sQuery(id+"F0.wireOp",EDGE,"E91.0.1.73"),sQuery(id+"F0.wireOp",EDGE,"E91.0.1.74"),sQuery(id+"F0.wireOp",EDGE,"E91.0.1.75"),sQuery(id+"F0.wireOp",EDGE,"E91.0.1.76"),sQuery(id+"F0.wireOp",EDGE,"E91.0.1.77"),sQuery(id+"F0.wireOp",EDGE,"E91.0.1.78"),sQuery(id+"F0.wireOp",EDGE,"E91.0.1.79"),sQuery(id+"F0.wireOp",EDGE,"E91.0.1.80"),sQuery(id+"F0.wireOp",EDGE,"E91.0.1.81"),sQuery(id+"F0.wireOp",EDGE,"E91.0.1.82"),sQuery(id+"F0.wireOp",EDGE,"E91.0.1.83"),sQuery(id+"F0.wireOp",EDGE,"E91.0.1.84"),sQuery(id+"F0.wireOp",EDGE,"E91.0.1.85"),sQuery(id+"F0.wireOp",EDGE,"E91.0.1.86"),sQuery(id+"F0.wireOp",EDGE,"E91.0.1.87"),sQuery(id+"F0.wireOp",EDGE,"E91.0.1.88"),sQuery(id+"F0.wireOp",EDGE,"E91.0.1.89"),sQuery(id+"F0.wireOp",EDGE,"E91.0.1.90"),sQuery(id+"F0.wireOp",EDGE,"E91.0.1.91"),sQuery(id+"F0.wireOp",EDGE,"E91.0.1.92"),sQuery(id+"F0.wireOp",EDGE,"E91.0.1.93"),sQuery(id+"F0.wireOp",EDGE,"E91.0.1.94"),sQuery(id+"F0.wireOp",EDGE,"E91.0.1.95"),sQuery(id+"F0.wireOp",EDGE,"E91.0.1.96"),sQuery(id+"F0.wireOp",EDGE,"E91.0.1.97"),sQuery(id+"F0.wireOp",EDGE,"E91.0.1.99"),sQuery(id+"F0.wireOp",EDGE,"E91.0.1.100"),sQuery(id+"F0.wireOp",EDGE,"E91.0.1.101"),sQuery(id+"F0.wireOp",EDGE,"E91.0.1.103"),sQuery(id+"F0.wireOp",EDGE,"E91.0.1.104"),sQuery(id+"F0.wireOp",EDGE,"E91.0.1.105"),sQuery(id+"F0.wireOp",EDGE,"E91.0.1.106"),sQuery(id+"F0.wireOp",EDGE,"E91.0.1.107"),sQuery(id+"F0.wireOp",EDGE,"E91.0.1.108"),sQuery(id+"F0.wireOp",EDGE,"E91.0.1.109"),sQuery(id+"F0.wireOp",EDGE,"E91.0.1.110"),sQuery(id+"F0.wireOp",EDGE,"E91.0.1.111"),sQuery(id+"F0.wireOp",EDGE,"E91.0.1.112"),sQuery(id+"F0.wireOp",EDGE,"E91.0.1.114"),sQuery(id+"F0.wireOp",EDGE,"E91.0.1.115"),sQuery(id+"F0.wireOp",EDGE,"E91.0.1.116")])]});
            var Q6;
            Q6=makeQuery(id+"F3.opExtrude","SWEPT_BODY",BODY,{"disambiguationData":[OSD([sQuery(id+"F2.wireOp",EDGE,"E92.bottom"),sQuery(id+"F2.wireOp",EDGE,"E92.top"),sQuery(id+"F2.wireOp",EDGE,"E92.left"),sQuery(id+"F2.wireOp",EDGE,"E92.right")])]});
            booleanBodies(context, id + "F5", {"operationType" : BooleanOperationType.SUBTRACTION, "tools" : qUnion([Q0, Q1, Q2, Q3, Q4, Q5]), "targets" : qUnion([Q6])});
        }
    });
